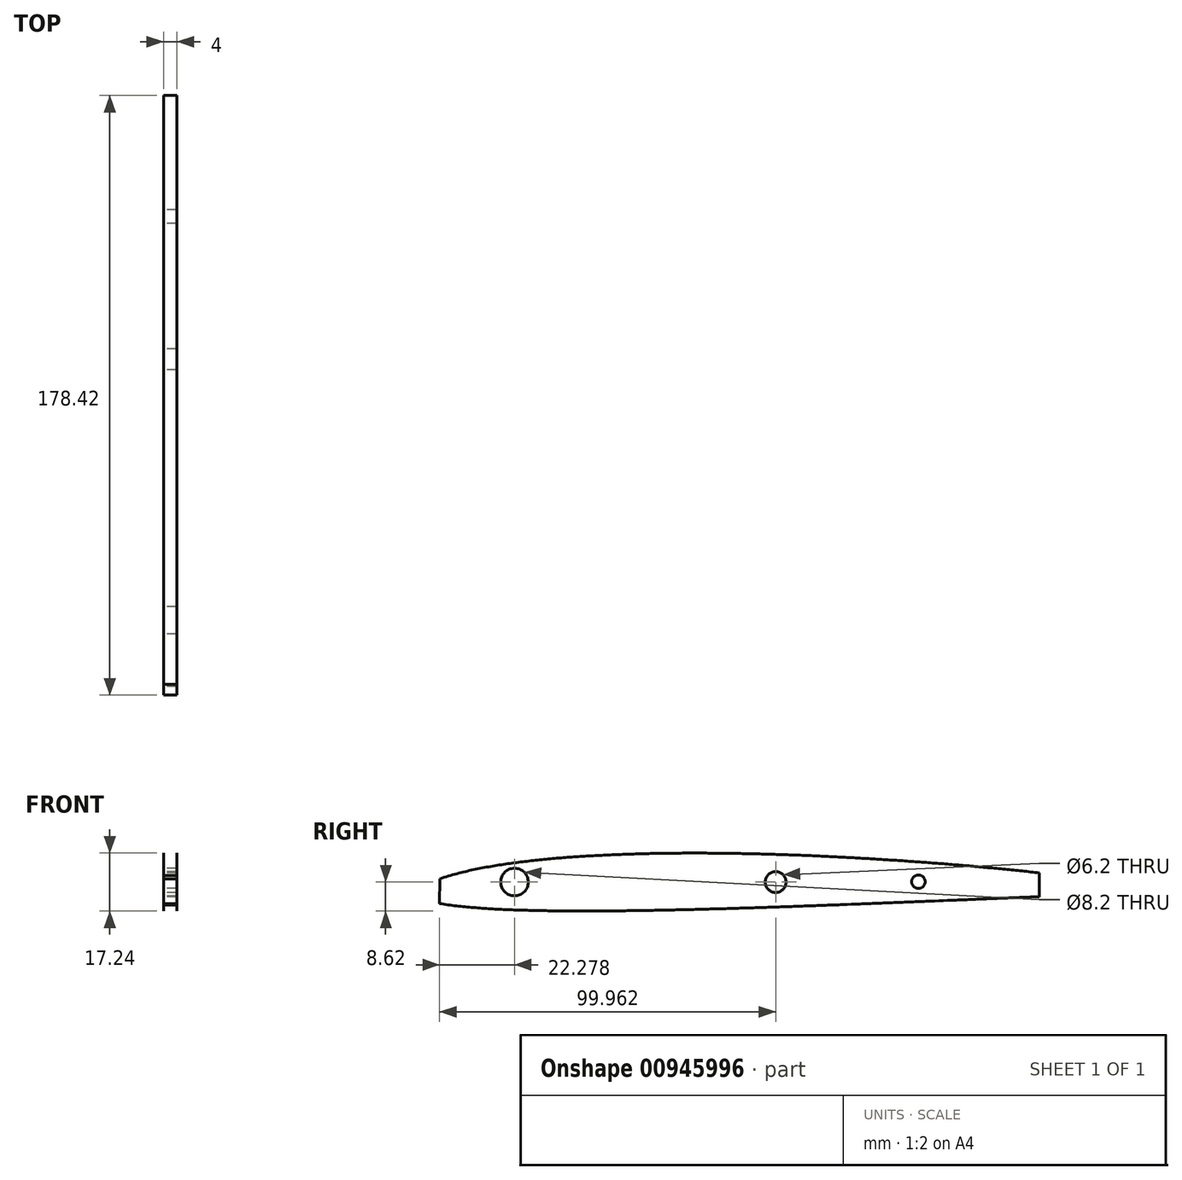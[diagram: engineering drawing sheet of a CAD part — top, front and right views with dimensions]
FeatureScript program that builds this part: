
annotation { "Feature Type Name" : "Feature", "Feature Type Description" : "" }
export const myFeature = defineFeature(function(context is Context, id is Id, definition is map)
    precondition{}
    {
        {
            var Q0;
            Q0=qCreatedBy(makeId("Right.planeOp"),FACE);
            var sketch = newSketch(context, id + "F0", { "sketchPlane" : qUnion([Q0])});
            skLineSegment(sketch, "E0", {"start": v(127, -3.95) * mm, "end": v(126.92, -3.95) * mm});
            skLineSegment(sketch, "E1", {"start": v(126.92, -3.95) * mm, "end": v(126.83, -3.94) * mm});
            skLineSegment(sketch, "E2", {"start": v(126.83, -3.94) * mm, "end": v(126.75, -3.93) * mm});
            skLineSegment(sketch, "E3", {"start": v(126.75, -3.93) * mm, "end": v(126.67, -3.93) * mm});
            skLineSegment(sketch, "E4", {"start": v(126.67, -3.93) * mm, "end": v(126.59, -3.92) * mm});
            skLineSegment(sketch, "E5", {"start": v(126.59, -3.92) * mm, "end": v(126.5, -3.91) * mm});
            skLineSegment(sketch, "E6", {"start": v(126.5, -3.91) * mm, "end": v(126.42, -3.9) * mm});
            skLineSegment(sketch, "E7", {"start": v(126.42, -3.9) * mm, "end": v(126.34, -3.9) * mm});
            skLineSegment(sketch, "E8", {"start": v(126.34, -3.9) * mm, "end": v(126.26, -3.9) * mm});
            skLineSegment(sketch, "E9", {"start": v(126.26, -3.9) * mm, "end": v(125.93, -3.86) * mm});
            skLineSegment(sketch, "E10", {"start": v(125.93, -3.86) * mm, "end": v(125.69, -3.84) * mm});
            skLineSegment(sketch, "E11", {"start": v(125.69, -3.84) * mm, "end": v(125.44, -3.82) * mm});
            skLineSegment(sketch, "E12", {"start": v(125.44, -3.82) * mm, "end": v(125.2, -3.8) * mm});
            skLineSegment(sketch, "E13", {"start": v(125.2, -3.8) * mm, "end": v(124.96, -3.77) * mm});
            skLineSegment(sketch, "E14", {"start": v(124.96, -3.77) * mm, "end": v(124.71, -3.75) * mm});
            skLineSegment(sketch, "E15", {"start": v(124.71, -3.75) * mm, "end": v(124.47, -3.72) * mm});
            skLineSegment(sketch, "E16", {"start": v(124.47, -3.72) * mm, "end": v(124.23, -3.7) * mm});
            skLineSegment(sketch, "E17", {"start": v(124.23, -3.7) * mm, "end": v(123.98, -3.67) * mm});
            skLineSegment(sketch, "E18", {"start": v(123.98, -3.67) * mm, "end": v(123.35, -3.6) * mm});
            skLineSegment(sketch, "E19", {"start": v(123.35, -3.6) * mm, "end": v(122.95, -3.56) * mm});
            skLineSegment(sketch, "E20", {"start": v(122.95, -3.56) * mm, "end": v(122.56, -3.52) * mm});
            skLineSegment(sketch, "E21", {"start": v(122.56, -3.52) * mm, "end": v(122.17, -3.48) * mm});
            skLineSegment(sketch, "E22", {"start": v(122.17, -3.48) * mm, "end": v(121.77, -3.43) * mm});
            skLineSegment(sketch, "E23", {"start": v(121.77, -3.43) * mm, "end": v(121.38, -3.39) * mm});
            skLineSegment(sketch, "E24", {"start": v(121.38, -3.39) * mm, "end": v(120.98, -3.34) * mm});
            skLineSegment(sketch, "E25", {"start": v(120.98, -3.34) * mm, "end": v(120.59, -3.3) * mm});
            skLineSegment(sketch, "E26", {"start": v(120.59, -3.3) * mm, "end": v(120.2, -3.25) * mm});
            skLineSegment(sketch, "E27", {"start": v(120.2, -3.25) * mm, "end": v(119.8, -3.2) * mm});
            skLineSegment(sketch, "E28", {"start": v(119.8, -3.2) * mm, "end": v(119.27, -3.14) * mm});
            skLineSegment(sketch, "E29", {"start": v(119.27, -3.14) * mm, "end": v(118.73, -3.07) * mm});
            skLineSegment(sketch, "E30", {"start": v(118.73, -3.07) * mm, "end": v(118.2, -3) * mm});
            skLineSegment(sketch, "E31", {"start": v(118.2, -3) * mm, "end": v(117.67, -2.94) * mm});
            skLineSegment(sketch, "E32", {"start": v(117.67, -2.94) * mm, "end": v(117.13, -2.87) * mm});
            skLineSegment(sketch, "E33", {"start": v(117.13, -2.87) * mm, "end": v(116.6, -2.8) * mm});
            skLineSegment(sketch, "E34", {"start": v(116.6, -2.8) * mm, "end": v(116.07, -2.74) * mm});
            skLineSegment(sketch, "E35", {"start": v(116.07, -2.74) * mm, "end": v(115.53, -2.67) * mm});
            skLineSegment(sketch, "E36", {"start": v(115.53, -2.67) * mm, "end": v(115, -2.6) * mm});
            skLineSegment(sketch, "E37", {"start": v(115, -2.6) * mm, "end": v(114.47, -2.54) * mm});
            skLineSegment(sketch, "E38", {"start": v(114.47, -2.54) * mm, "end": v(113.8, -2.45) * mm});
            skLineSegment(sketch, "E39", {"start": v(113.8, -2.45) * mm, "end": v(113.14, -2.37) * mm});
            skLineSegment(sketch, "E40", {"start": v(113.14, -2.37) * mm, "end": v(112.48, -2.28) * mm});
            skLineSegment(sketch, "E41", {"start": v(112.48, -2.28) * mm, "end": v(111.82, -2.2) * mm});
            skLineSegment(sketch, "E42", {"start": v(111.82, -2.2) * mm, "end": v(111.16, -2.1) * mm});
            skLineSegment(sketch, "E43", {"start": v(111.16, -2.1) * mm, "end": v(110.5, -2.02) * mm});
            skLineSegment(sketch, "E44", {"start": v(110.5, -2.02) * mm, "end": v(109.84, -1.93) * mm});
            skLineSegment(sketch, "E45", {"start": v(109.84, -1.93) * mm, "end": v(109.17, -1.84) * mm});
            skLineSegment(sketch, "E46", {"start": v(109.17, -1.84) * mm, "end": v(108.51, -1.75) * mm});
            skLineSegment(sketch, "E47", {"start": v(108.51, -1.75) * mm, "end": v(107.07, -1.56) * mm});
            skLineSegment(sketch, "E48", {"start": v(107.07, -1.56) * mm, "end": v(106.3, -1.46) * mm});
            skLineSegment(sketch, "E49", {"start": v(106.3, -1.46) * mm, "end": v(105.52, -1.35) * mm});
            skLineSegment(sketch, "E50", {"start": v(105.52, -1.35) * mm, "end": v(104.74, -1.25) * mm});
            skLineSegment(sketch, "E51", {"start": v(104.74, -1.25) * mm, "end": v(103.96, -1.14) * mm});
            skLineSegment(sketch, "E52", {"start": v(103.96, -1.14) * mm, "end": v(103.19, -1.04) * mm});
            skLineSegment(sketch, "E53", {"start": v(103.19, -1.04) * mm, "end": v(102.4, -0.93) * mm});
            skLineSegment(sketch, "E54", {"start": v(102.4, -0.93) * mm, "end": v(101.63, -0.82) * mm});
            skLineSegment(sketch, "E55", {"start": v(101.63, -0.82) * mm, "end": v(100.85, -0.72) * mm});
            skLineSegment(sketch, "E56", {"start": v(100.85, -0.72) * mm, "end": v(100.08, -0.61) * mm});
            skLineSegment(sketch, "E57", {"start": v(100.08, -0.61) * mm, "end": v(99.2, -0.5) * mm});
            skLineSegment(sketch, "E58", {"start": v(99.2, -0.5) * mm, "end": v(98.32, -0.38) * mm});
            skLineSegment(sketch, "E59", {"start": v(98.32, -0.38) * mm, "end": v(97.43, -0.26) * mm});
            skLineSegment(sketch, "E60", {"start": v(97.43, -0.26) * mm, "end": v(96.55, -0.14) * mm});
            skLineSegment(sketch, "E61", {"start": v(96.55, -0.14) * mm, "end": v(95.67, -0.02) * mm});
            skLineSegment(sketch, "E62", {"start": v(95.67, -0.02) * mm, "end": v(94.8, 0.1) * mm});
            skLineSegment(sketch, "E63", {"start": v(94.8, 0.1) * mm, "end": v(93.91, 0.22) * mm});
            skLineSegment(sketch, "E64", {"start": v(93.91, 0.22) * mm, "end": v(93.03, 0.34) * mm});
            skLineSegment(sketch, "E65", {"start": v(93.03, 0.34) * mm, "end": v(92.15, 0.45) * mm});
            skLineSegment(sketch, "E66", {"start": v(92.15, 0.45) * mm, "end": v(90.3, 0.7) * mm});
            skLineSegment(sketch, "E67", {"start": v(90.3, 0.7) * mm, "end": v(89.33, 0.83) * mm});
            skLineSegment(sketch, "E68", {"start": v(89.33, 0.83) * mm, "end": v(88.36, 0.96) * mm});
            skLineSegment(sketch, "E69", {"start": v(88.36, 0.96) * mm, "end": v(87.39, 1.09) * mm});
            skLineSegment(sketch, "E70", {"start": v(87.39, 1.09) * mm, "end": v(86.42, 1.22) * mm});
            skLineSegment(sketch, "E71", {"start": v(86.42, 1.22) * mm, "end": v(85.44, 1.34) * mm});
            skLineSegment(sketch, "E72", {"start": v(85.44, 1.34) * mm, "end": v(84.47, 1.47) * mm});
            skLineSegment(sketch, "E73", {"start": v(84.47, 1.47) * mm, "end": v(83.5, 1.6) * mm});
            skLineSegment(sketch, "E74", {"start": v(83.5, 1.6) * mm, "end": v(82.53, 1.72) * mm});
            skLineSegment(sketch, "E75", {"start": v(82.53, 1.72) * mm, "end": v(81.56, 1.85) * mm});
            skLineSegment(sketch, "E76", {"start": v(81.56, 1.85) * mm, "end": v(80.51, 1.98) * mm});
            skLineSegment(sketch, "E77", {"start": v(80.51, 1.98) * mm, "end": v(79.46, 2.12) * mm});
            skLineSegment(sketch, "E78", {"start": v(79.46, 2.12) * mm, "end": v(78.41, 2.25) * mm});
            skLineSegment(sketch, "E79", {"start": v(78.41, 2.25) * mm, "end": v(77.36, 2.38) * mm});
            skLineSegment(sketch, "E80", {"start": v(77.36, 2.38) * mm, "end": v(76.31, 2.51) * mm});
            skLineSegment(sketch, "E81", {"start": v(76.31, 2.51) * mm, "end": v(75.26, 2.64) * mm});
            skLineSegment(sketch, "E82", {"start": v(75.26, 2.64) * mm, "end": v(74.21, 2.77) * mm});
            skLineSegment(sketch, "E83", {"start": v(74.21, 2.77) * mm, "end": v(73.17, 2.9) * mm});
            skLineSegment(sketch, "E84", {"start": v(73.17, 2.9) * mm, "end": v(72.12, 3.03) * mm});
            skLineSegment(sketch, "E85", {"start": v(72.12, 3.03) * mm, "end": v(69.95, 3.29) * mm});
            skLineSegment(sketch, "E86", {"start": v(69.95, 3.29) * mm, "end": v(68.83, 3.42) * mm});
            skLineSegment(sketch, "E87", {"start": v(68.83, 3.42) * mm, "end": v(67.72, 3.55) * mm});
            skLineSegment(sketch, "E88", {"start": v(67.72, 3.55) * mm, "end": v(66.6, 3.68) * mm});
            skLineSegment(sketch, "E89", {"start": v(66.6, 3.68) * mm, "end": v(65.48, 3.8) * mm});
            skLineSegment(sketch, "E90", {"start": v(65.48, 3.8) * mm, "end": v(64.37, 3.93) * mm});
            skLineSegment(sketch, "E91", {"start": v(64.37, 3.93) * mm, "end": v(63.25, 4.06) * mm});
            skLineSegment(sketch, "E92", {"start": v(63.25, 4.06) * mm, "end": v(62.14, 4.18) * mm});
            skLineSegment(sketch, "E93", {"start": v(62.14, 4.18) * mm, "end": v(61.02, 4.3) * mm});
            skLineSegment(sketch, "E94", {"start": v(61.02, 4.3) * mm, "end": v(58.73, 4.55) * mm});
            skLineSegment(sketch, "E95", {"start": v(58.73, 4.55) * mm, "end": v(57.56, 4.68) * mm});
            skLineSegment(sketch, "E96", {"start": v(57.56, 4.68) * mm, "end": v(56.38, 4.8) * mm});
            skLineSegment(sketch, "E97", {"start": v(56.38, 4.8) * mm, "end": v(55.21, 4.92) * mm});
            skLineSegment(sketch, "E98", {"start": v(55.21, 4.92) * mm, "end": v(54.04, 5.04) * mm});
            skLineSegment(sketch, "E99", {"start": v(54.04, 5.04) * mm, "end": v(52.86, 5.16) * mm});
            skLineSegment(sketch, "E100", {"start": v(52.86, 5.16) * mm, "end": v(51.7, 5.27) * mm});
            skLineSegment(sketch, "E101", {"start": v(51.7, 5.27) * mm, "end": v(50.52, 5.39) * mm});
            skLineSegment(sketch, "E102", {"start": v(50.52, 5.39) * mm, "end": v(49.34, 5.5) * mm});
            skLineSegment(sketch, "E103", {"start": v(49.34, 5.5) * mm, "end": v(48.17, 5.61) * mm});
            skLineSegment(sketch, "E104", {"start": v(48.17, 5.61) * mm, "end": v(46.95, 5.73) * mm});
            skLineSegment(sketch, "E105", {"start": v(46.95, 5.73) * mm, "end": v(45.73, 5.84) * mm});
            skLineSegment(sketch, "E106", {"start": v(45.73, 5.84) * mm, "end": v(44.51, 5.95) * mm});
            skLineSegment(sketch, "E107", {"start": v(44.51, 5.95) * mm, "end": v(43.3, 6.06) * mm});
            skLineSegment(sketch, "E108", {"start": v(43.3, 6.06) * mm, "end": v(42.07, 6.17) * mm});
            skLineSegment(sketch, "E109", {"start": v(42.07, 6.17) * mm, "end": v(40.85, 6.28) * mm});
            skLineSegment(sketch, "E110", {"start": v(40.85, 6.28) * mm, "end": v(39.63, 6.39) * mm});
            skLineSegment(sketch, "E111", {"start": v(39.63, 6.39) * mm, "end": v(38.41, 6.5) * mm});
            skLineSegment(sketch, "E112", {"start": v(38.41, 6.5) * mm, "end": v(37.2, 6.6) * mm});
            skLineSegment(sketch, "E113", {"start": v(37.2, 6.6) * mm, "end": v(35.97, 6.7) * mm});
            skLineSegment(sketch, "E114", {"start": v(35.97, 6.7) * mm, "end": v(34.72, 6.8) * mm});
            skLineSegment(sketch, "E115", {"start": v(34.72, 6.8) * mm, "end": v(33.46, 6.9) * mm});
            skLineSegment(sketch, "E116", {"start": v(33.46, 6.9) * mm, "end": v(32.2, 7) * mm});
            skLineSegment(sketch, "E117", {"start": v(32.2, 7) * mm, "end": v(30.95, 7.1) * mm});
            skLineSegment(sketch, "E118", {"start": v(30.95, 7.1) * mm, "end": v(29.7, 7.2) * mm});
            skLineSegment(sketch, "E119", {"start": v(29.7, 7.2) * mm, "end": v(28.44, 7.29) * mm});
            skLineSegment(sketch, "E120", {"start": v(28.44, 7.29) * mm, "end": v(27.19, 7.38) * mm});
            skLineSegment(sketch, "E121", {"start": v(27.19, 7.38) * mm, "end": v(25.93, 7.47) * mm});
            skLineSegment(sketch, "E122", {"start": v(25.93, 7.47) * mm, "end": v(24.68, 7.56) * mm});
            skLineSegment(sketch, "E123", {"start": v(24.68, 7.56) * mm, "end": v(23.42, 7.65) * mm});
            skLineSegment(sketch, "E124", {"start": v(23.42, 7.65) * mm, "end": v(22.15, 7.74) * mm});
            skLineSegment(sketch, "E125", {"start": v(22.15, 7.74) * mm, "end": v(20.87, 7.83) * mm});
            skLineSegment(sketch, "E126", {"start": v(20.87, 7.83) * mm, "end": v(19.6, 7.91) * mm});
            skLineSegment(sketch, "E127", {"start": v(19.6, 7.91) * mm, "end": v(18.31, 8) * mm});
            skLineSegment(sketch, "E128", {"start": v(18.31, 8) * mm, "end": v(17.04, 8.08) * mm});
            skLineSegment(sketch, "E129", {"start": v(17.04, 8.08) * mm, "end": v(15.76, 8.16) * mm});
            skLineSegment(sketch, "E130", {"start": v(15.76, 8.16) * mm, "end": v(14.48, 8.24) * mm});
            skLineSegment(sketch, "E131", {"start": v(14.48, 8.24) * mm, "end": v(13.2, 8.32) * mm});
            skLineSegment(sketch, "E132", {"start": v(13.2, 8.32) * mm, "end": v(11.93, 8.4) * mm});
            skLineSegment(sketch, "E133", {"start": v(11.93, 8.4) * mm, "end": v(9.37, 8.55) * mm});
            skLineSegment(sketch, "E134", {"start": v(9.37, 8.55) * mm, "end": v(8.08, 8.63) * mm});
            skLineSegment(sketch, "E135", {"start": v(8.08, 8.63) * mm, "end": v(6.8, 8.7) * mm});
            skLineSegment(sketch, "E136", {"start": v(6.8, 8.7) * mm, "end": v(5.51, 8.77) * mm});
            skLineSegment(sketch, "E137", {"start": v(5.51, 8.77) * mm, "end": v(4.23, 8.84) * mm});
            skLineSegment(sketch, "E138", {"start": v(4.23, 8.84) * mm, "end": v(2.94, 8.9) * mm});
            skLineSegment(sketch, "E139", {"start": v(2.94, 8.9) * mm, "end": v(1.66, 8.97) * mm});
            skLineSegment(sketch, "E140", {"start": v(1.66, 8.97) * mm, "end": v(0.38, 9.04) * mm});
            skLineSegment(sketch, "E141", {"start": v(0.38, 9.04) * mm, "end": v(-0.9, 9.1) * mm});
            skLineSegment(sketch, "E142", {"start": v(-0.9, 9.1) * mm, "end": v(-3.47, 9.22) * mm});
            skLineSegment(sketch, "E143", {"start": v(-3.47, 9.22) * mm, "end": v(-4.75, 9.28) * mm});
            skLineSegment(sketch, "E144", {"start": v(-4.75, 9.28) * mm, "end": v(-6.02, 9.33) * mm});
            skLineSegment(sketch, "E145", {"start": v(-6.02, 9.33) * mm, "end": v(-7.3, 9.39) * mm});
            skLineSegment(sketch, "E146", {"start": v(-7.3, 9.39) * mm, "end": v(-8.58, 9.44) * mm});
            skLineSegment(sketch, "E147", {"start": v(-8.58, 9.44) * mm, "end": v(-9.86, 9.5) * mm});
            skLineSegment(sketch, "E148", {"start": v(-9.86, 9.5) * mm, "end": v(-11.14, 9.54) * mm});
            skLineSegment(sketch, "E149", {"start": v(-11.14, 9.54) * mm, "end": v(-12.41, 9.59) * mm});
            skLineSegment(sketch, "E150", {"start": v(-12.41, 9.59) * mm, "end": v(-13.7, 9.63) * mm});
            skLineSegment(sketch, "E151", {"start": v(-13.7, 9.63) * mm, "end": v(-16.23, 9.71) * mm});
            skLineSegment(sketch, "E152", {"start": v(-16.23, 9.71) * mm, "end": v(-17.49, 9.75) * mm});
            skLineSegment(sketch, "E153", {"start": v(-17.49, 9.75) * mm, "end": v(-18.74, 9.79) * mm});
            skLineSegment(sketch, "E154", {"start": v(-18.74, 9.79) * mm, "end": v(-20, 9.82) * mm});
            skLineSegment(sketch, "E155", {"start": v(-20, 9.82) * mm, "end": v(-21.26, 9.86) * mm});
            skLineSegment(sketch, "E156", {"start": v(-21.26, 9.86) * mm, "end": v(-22.52, 9.89) * mm});
            skLineSegment(sketch, "E157", {"start": v(-22.52, 9.89) * mm, "end": v(-23.78, 9.92) * mm});
            skLineSegment(sketch, "E158", {"start": v(-23.78, 9.92) * mm, "end": v(-25.04, 9.94) * mm});
            skLineSegment(sketch, "E159", {"start": v(-25.04, 9.94) * mm, "end": v(-26.3, 9.97) * mm});
            skLineSegment(sketch, "E160", {"start": v(-26.3, 9.97) * mm, "end": v(-28.78, 10.01) * mm});
            skLineSegment(sketch, "E161", {"start": v(-28.78, 10.01) * mm, "end": v(-30.01, 10.03) * mm});
            skLineSegment(sketch, "E162", {"start": v(-30.01, 10.03) * mm, "end": v(-31.24, 10.05) * mm});
            skLineSegment(sketch, "E163", {"start": v(-31.24, 10.05) * mm, "end": v(-32.47, 10.07) * mm});
            skLineSegment(sketch, "E164", {"start": v(-32.47, 10.07) * mm, "end": v(-33.7, 10.08) * mm});
            skLineSegment(sketch, "E165", {"start": v(-33.7, 10.08) * mm, "end": v(-34.92, 10.1) * mm});
            skLineSegment(sketch, "E166", {"start": v(-34.92, 10.1) * mm, "end": v(-36.15, 10.1) * mm});
            skLineSegment(sketch, "E167", {"start": v(-36.15, 10.1) * mm, "end": v(-37.38, 10.1) * mm});
            skLineSegment(sketch, "E168", {"start": v(-37.38, 10.1) * mm, "end": v(-38.6, 10.11) * mm});
            skLineSegment(sketch, "E169", {"start": v(-38.6, 10.11) * mm, "end": v(-39.83, 10.12) * mm});
            skLineSegment(sketch, "E170", {"start": v(-39.83, 10.12) * mm, "end": v(-41.01, 10.12) * mm});
            skLineSegment(sketch, "E171", {"start": v(-41.01, 10.12) * mm, "end": v(-42.2, 10.12) * mm});
            skLineSegment(sketch, "E172", {"start": v(-42.2, 10.12) * mm, "end": v(-43.38, 10.11) * mm});
            skLineSegment(sketch, "E173", {"start": v(-43.38, 10.11) * mm, "end": v(-44.56, 10.1) * mm});
            skLineSegment(sketch, "E174", {"start": v(-44.56, 10.1) * mm, "end": v(-45.74, 10.1) * mm});
            skLineSegment(sketch, "E175", {"start": v(-45.74, 10.1) * mm, "end": v(-46.93, 10.09) * mm});
            skLineSegment(sketch, "E176", {"start": v(-46.93, 10.09) * mm, "end": v(-48.1, 10.08) * mm});
            skLineSegment(sketch, "E177", {"start": v(-48.1, 10.08) * mm, "end": v(-49.3, 10.06) * mm});
            skLineSegment(sketch, "E178", {"start": v(-49.3, 10.06) * mm, "end": v(-50.47, 10.05) * mm});
            skLineSegment(sketch, "E179", {"start": v(-50.47, 10.05) * mm, "end": v(-51.66, 10.03) * mm});
            skLineSegment(sketch, "E180", {"start": v(-51.66, 10.03) * mm, "end": v(-52.78, 10) * mm});
            skLineSegment(sketch, "E181", {"start": v(-52.78, 10) * mm, "end": v(-53.91, 9.98) * mm});
            skLineSegment(sketch, "E182", {"start": v(-53.91, 9.98) * mm, "end": v(-55.04, 9.96) * mm});
            skLineSegment(sketch, "E183", {"start": v(-55.04, 9.96) * mm, "end": v(-56.17, 9.93) * mm});
            skLineSegment(sketch, "E184", {"start": v(-56.17, 9.93) * mm, "end": v(-57.3, 9.9) * mm});
            skLineSegment(sketch, "E185", {"start": v(-57.3, 9.9) * mm, "end": v(-58.42, 9.87) * mm});
            skLineSegment(sketch, "E186", {"start": v(-58.42, 9.87) * mm, "end": v(-59.55, 9.83) * mm});
            skLineSegment(sketch, "E187", {"start": v(-59.55, 9.83) * mm, "end": v(-60.68, 9.8) * mm});
            skLineSegment(sketch, "E188", {"start": v(-60.68, 9.8) * mm, "end": v(-61.8, 9.76) * mm});
            skLineSegment(sketch, "E189", {"start": v(-61.8, 9.76) * mm, "end": v(-62.93, 9.72) * mm});
            skLineSegment(sketch, "E190", {"start": v(-62.93, 9.72) * mm, "end": v(-64, 9.68) * mm});
            skLineSegment(sketch, "E191", {"start": v(-64, 9.68) * mm, "end": v(-65.05, 9.63) * mm});
            skLineSegment(sketch, "E192", {"start": v(-65.05, 9.63) * mm, "end": v(-66.11, 9.59) * mm});
            skLineSegment(sketch, "E193", {"start": v(-66.11, 9.59) * mm, "end": v(-67.18, 9.54) * mm});
            skLineSegment(sketch, "E194", {"start": v(-67.18, 9.54) * mm, "end": v(-68.24, 9.49) * mm});
            skLineSegment(sketch, "E195", {"start": v(-68.24, 9.49) * mm, "end": v(-69.3, 9.43) * mm});
            skLineSegment(sketch, "E196", {"start": v(-69.3, 9.43) * mm, "end": v(-70.36, 9.38) * mm});
            skLineSegment(sketch, "E197", {"start": v(-70.36, 9.38) * mm, "end": v(-71.42, 9.32) * mm});
            skLineSegment(sketch, "E198", {"start": v(-71.42, 9.32) * mm, "end": v(-72.48, 9.26) * mm});
            skLineSegment(sketch, "E199", {"start": v(-72.48, 9.26) * mm, "end": v(-74.53, 9.13) * mm});
            skLineSegment(sketch, "E200", {"start": v(-74.53, 9.13) * mm, "end": v(-75.51, 9.07) * mm});
            skLineSegment(sketch, "E201", {"start": v(-75.51, 9.07) * mm, "end": v(-76.5, 9) * mm});
            skLineSegment(sketch, "E202", {"start": v(-76.5, 9) * mm, "end": v(-77.48, 8.93) * mm});
            skLineSegment(sketch, "E203", {"start": v(-77.48, 8.93) * mm, "end": v(-78.46, 8.86) * mm});
            skLineSegment(sketch, "E204", {"start": v(-78.46, 8.86) * mm, "end": v(-79.45, 8.79) * mm});
            skLineSegment(sketch, "E205", {"start": v(-79.45, 8.79) * mm, "end": v(-80.43, 8.71) * mm});
            skLineSegment(sketch, "E206", {"start": v(-80.43, 8.71) * mm, "end": v(-81.42, 8.63) * mm});
            skLineSegment(sketch, "E207", {"start": v(-81.42, 8.63) * mm, "end": v(-82.4, 8.55) * mm});
            skLineSegment(sketch, "E208", {"start": v(-82.4, 8.55) * mm, "end": v(-84.28, 8.38) * mm});
            skLineSegment(sketch, "E209", {"start": v(-84.28, 8.38) * mm, "end": v(-85.18, 8.3) * mm});
            skLineSegment(sketch, "E210", {"start": v(-85.18, 8.3) * mm, "end": v(-86.08, 8.2) * mm});
            skLineSegment(sketch, "E211", {"start": v(-86.08, 8.2) * mm, "end": v(-86.98, 8.11) * mm});
            skLineSegment(sketch, "E212", {"start": v(-86.98, 8.11) * mm, "end": v(-87.88, 8.02) * mm});
            skLineSegment(sketch, "E213", {"start": v(-87.88, 8.02) * mm, "end": v(-88.77, 7.92) * mm});
            skLineSegment(sketch, "E214", {"start": v(-88.77, 7.92) * mm, "end": v(-89.67, 7.82) * mm});
            skLineSegment(sketch, "E215", {"start": v(-89.67, 7.82) * mm, "end": v(-90.57, 7.72) * mm});
            skLineSegment(sketch, "E216", {"start": v(-90.57, 7.72) * mm, "end": v(-91.47, 7.61) * mm});
            skLineSegment(sketch, "E217", {"start": v(-91.47, 7.61) * mm, "end": v(-92.37, 7.5) * mm});
            skLineSegment(sketch, "E218", {"start": v(-92.37, 7.5) * mm, "end": v(-93.17, 7.4) * mm});
            skLineSegment(sketch, "E219", {"start": v(-93.17, 7.4) * mm, "end": v(-93.98, 7.3) * mm});
            skLineSegment(sketch, "E220", {"start": v(-93.98, 7.3) * mm, "end": v(-94.78, 7.2) * mm});
            skLineSegment(sketch, "E221", {"start": v(-94.78, 7.2) * mm, "end": v(-95.59, 7.08) * mm});
            skLineSegment(sketch, "E222", {"start": v(-95.59, 7.08) * mm, "end": v(-96.4, 6.97) * mm});
            skLineSegment(sketch, "E223", {"start": v(-96.4, 6.97) * mm, "end": v(-97.2, 6.85) * mm});
            skLineSegment(sketch, "E224", {"start": v(-97.2, 6.85) * mm, "end": v(-98, 6.73) * mm});
            skLineSegment(sketch, "E225", {"start": v(-98, 6.73) * mm, "end": v(-98.81, 6.6) * mm});
            skLineSegment(sketch, "E226", {"start": v(-98.81, 6.6) * mm, "end": v(-99.62, 6.48) * mm});
            skLineSegment(sketch, "E227", {"start": v(-99.62, 6.48) * mm, "end": v(-100.42, 6.35) * mm});
            skLineSegment(sketch, "E228", {"start": v(-100.42, 6.35) * mm, "end": v(-101.13, 6.23) * mm});
            skLineSegment(sketch, "E229", {"start": v(-101.13, 6.23) * mm, "end": v(-101.83, 6.1) * mm});
            skLineSegment(sketch, "E230", {"start": v(-101.83, 6.1) * mm, "end": v(-102.54, 5.98) * mm});
            skLineSegment(sketch, "E231", {"start": v(-102.54, 5.98) * mm, "end": v(-103.25, 5.85) * mm});
            skLineSegment(sketch, "E232", {"start": v(-103.25, 5.85) * mm, "end": v(-103.95, 5.72) * mm});
            skLineSegment(sketch, "E233", {"start": v(-103.95, 5.72) * mm, "end": v(-104.66, 5.59) * mm});
            skLineSegment(sketch, "E234", {"start": v(-104.66, 5.59) * mm, "end": v(-105.37, 5.45) * mm});
            skLineSegment(sketch, "E235", {"start": v(-105.37, 5.45) * mm, "end": v(-106.07, 5.3) * mm});
            skLineSegment(sketch, "E236", {"start": v(-106.07, 5.3) * mm, "end": v(-106.78, 5.16) * mm});
            skLineSegment(sketch, "E237", {"start": v(-108.09, 4.87) * mm, "end": v(-108.69, 4.73) * mm});
            skLineSegment(sketch, "E238", {"start": v(-108.69, 4.73) * mm, "end": v(-109.3, 4.6) * mm});
            skLineSegment(sketch, "E239", {"start": v(-109.3, 4.6) * mm, "end": v(-109.9, 4.45) * mm});
            skLineSegment(sketch, "E240", {"start": v(-109.9, 4.45) * mm, "end": v(-110.5, 4.3) * mm});
            skLineSegment(sketch, "E241", {"start": v(-110.5, 4.3) * mm, "end": v(-111.1, 4.15) * mm});
            skLineSegment(sketch, "E242", {"start": v(-111.1, 4.15) * mm, "end": v(-111.7, 4) * mm});
            skLineSegment(sketch, "E243", {"start": v(-111.7, 4) * mm, "end": v(-112.3, 3.84) * mm});
            skLineSegment(sketch, "E244", {"start": v(-112.3, 3.84) * mm, "end": v(-112.9, 3.67) * mm});
            skLineSegment(sketch, "E245", {"start": v(-112.9, 3.67) * mm, "end": v(-113.5, 3.5) * mm});
            skLineSegment(sketch, "E246", {"start": v(-113.5, 3.5) * mm, "end": v(-114, 3.36) * mm});
            skLineSegment(sketch, "E247", {"start": v(-114, 3.36) * mm, "end": v(-114.5, 3.21) * mm});
            skLineSegment(sketch, "E248", {"start": v(-114.5, 3.21) * mm, "end": v(-115, 3.06) * mm});
            skLineSegment(sketch, "E249", {"start": v(-115, 3.06) * mm, "end": v(-115.49, 2.9) * mm});
            skLineSegment(sketch, "E250", {"start": v(-115.49, 2.9) * mm, "end": v(-115.98, 2.74) * mm});
            skLineSegment(sketch, "E251", {"start": v(-115.98, 2.74) * mm, "end": v(-116.48, 2.58) * mm});
            skLineSegment(sketch, "E252", {"start": v(-116.48, 2.58) * mm, "end": v(-116.97, 2.41) * mm});
            skLineSegment(sketch, "E253", {"start": v(-116.97, 2.41) * mm, "end": v(-117.47, 2.24) * mm});
            skLineSegment(sketch, "E254", {"start": v(-117.47, 2.24) * mm, "end": v(-117.96, 2.06) * mm});
            skLineSegment(sketch, "E255", {"start": v(-117.96, 2.06) * mm, "end": v(-118.46, 1.88) * mm});
            skLineSegment(sketch, "E256", {"start": v(-118.46, 1.88) * mm, "end": v(-118.9, 1.71) * mm});
            skLineSegment(sketch, "E257", {"start": v(-118.9, 1.71) * mm, "end": v(-119.32, 1.54) * mm});
            skLineSegment(sketch, "E258", {"start": v(-119.32, 1.54) * mm, "end": v(-119.74, 1.37) * mm});
            skLineSegment(sketch, "E259", {"start": v(-119.74, 1.37) * mm, "end": v(-120.14, 1.2) * mm});
            skLineSegment(sketch, "E260", {"start": v(-120.14, 1.2) * mm, "end": v(-120.53, 1.03) * mm});
            skLineSegment(sketch, "E261", {"start": v(-120.53, 1.03) * mm, "end": v(-120.9, 0.86) * mm});
            skLineSegment(sketch, "E262", {"start": v(-120.9, 0.86) * mm, "end": v(-121.27, 0.7) * mm});
            skLineSegment(sketch, "E263", {"start": v(-121.27, 0.7) * mm, "end": v(-121.63, 0.53) * mm});
            skLineSegment(sketch, "E264", {"start": v(-121.63, 0.53) * mm, "end": v(-121.97, 0.36) * mm});
            skLineSegment(sketch, "E265", {"start": v(-121.97, 0.36) * mm, "end": v(-122.3, 0.19) * mm});
            skLineSegment(sketch, "E266", {"start": v(-122.3, 0.19) * mm, "end": v(-122.62, 0.02) * mm});
            skLineSegment(sketch, "E267", {"start": v(-122.62, 0.02) * mm, "end": v(-122.93, -0.15) * mm});
            skLineSegment(sketch, "E268", {"start": v(-122.93, -0.15) * mm, "end": v(-123.23, -0.32) * mm});
            skLineSegment(sketch, "E269", {"start": v(-123.23, -0.32) * mm, "end": v(-123.52, -0.49) * mm});
            skLineSegment(sketch, "E270", {"start": v(-123.52, -0.49) * mm, "end": v(-123.8, -0.66) * mm});
            skLineSegment(sketch, "E271", {"start": v(-123.8, -0.66) * mm, "end": v(-124.06, -0.83) * mm});
            skLineSegment(sketch, "E272", {"start": v(-124.06, -0.83) * mm, "end": v(-124.32, -1) * mm});
            skLineSegment(sketch, "E273", {"start": v(-124.32, -1) * mm, "end": v(-124.57, -1.16) * mm});
            skLineSegment(sketch, "E274", {"start": v(-124.57, -1.16) * mm, "end": v(-124.81, -1.33) * mm});
            skLineSegment(sketch, "E275", {"start": v(-124.81, -1.33) * mm, "end": v(-125.04, -1.5) * mm});
            skLineSegment(sketch, "E276", {"start": v(-125.04, -1.5) * mm, "end": v(-125.24, -1.66) * mm});
            skLineSegment(sketch, "E277", {"start": v(-125.24, -1.66) * mm, "end": v(-125.43, -1.81) * mm});
            skLineSegment(sketch, "E278", {"start": v(-125.43, -1.81) * mm, "end": v(-125.6, -1.97) * mm});
            skLineSegment(sketch, "E279", {"start": v(-125.6, -1.97) * mm, "end": v(-125.78, -2.13) * mm});
            skLineSegment(sketch, "E280", {"start": v(-125.78, -2.13) * mm, "end": v(-125.95, -2.28) * mm});
            skLineSegment(sketch, "E281", {"start": v(-125.95, -2.28) * mm, "end": v(-126.1, -2.44) * mm});
            skLineSegment(sketch, "E282", {"start": v(-126.1, -2.44) * mm, "end": v(-126.26, -2.6) * mm});
            skLineSegment(sketch, "E283", {"start": v(-126.26, -2.6) * mm, "end": v(-126.4, -2.75) * mm});
            skLineSegment(sketch, "E284", {"start": v(-126.4, -2.75) * mm, "end": v(-126.52, -2.91) * mm});
            skLineSegment(sketch, "E285", {"start": v(-126.52, -2.91) * mm, "end": v(-126.64, -3.07) * mm});
            skLineSegment(sketch, "E286", {"start": v(-126.64, -3.07) * mm, "end": v(-126.7, -3.16) * mm});
            skLineSegment(sketch, "E287", {"start": v(-126.7, -3.16) * mm, "end": v(-126.76, -3.24) * mm});
            skLineSegment(sketch, "E288", {"start": v(-126.76, -3.24) * mm, "end": v(-126.81, -3.33) * mm});
            skLineSegment(sketch, "E289", {"start": v(-126.81, -3.33) * mm, "end": v(-126.86, -3.42) * mm});
            skLineSegment(sketch, "E290", {"start": v(-126.86, -3.42) * mm, "end": v(-126.9, -3.51) * mm});
            skLineSegment(sketch, "E291", {"start": v(-126.9, -3.51) * mm, "end": v(-126.93, -3.6) * mm});
            skLineSegment(sketch, "E292", {"start": v(-126.93, -3.6) * mm, "end": v(-126.96, -3.69) * mm});
            skLineSegment(sketch, "E293", {"start": v(-126.96, -3.69) * mm, "end": v(-126.98, -3.78) * mm});
            skLineSegment(sketch, "E294", {"start": v(-126.98, -3.78) * mm, "end": v(-127, -3.87) * mm});
            skLineSegment(sketch, "E295", {"start": v(-127, -3.87) * mm, "end": v(-127, -3.95) * mm});
            skLineSegment(sketch, "E296", {"start": v(-127, -3.95) * mm, "end": v(-127, -3.99) * mm});
            skLineSegment(sketch, "E297", {"start": v(-127, -3.99) * mm, "end": v(-127, -4.02) * mm});
            skLineSegment(sketch, "E298", {"start": v(-127, -4.02) * mm, "end": v(-127, -4.06) * mm});
            skLineSegment(sketch, "E299", {"start": v(-127, -4.06) * mm, "end": v(-127, -4.1) * mm});
            skLineSegment(sketch, "E300", {"start": v(-127, -4.1) * mm, "end": v(-126.99, -4.13) * mm});
            skLineSegment(sketch, "E301", {"start": v(-126.99, -4.13) * mm, "end": v(-126.98, -4.16) * mm});
            skLineSegment(sketch, "E302", {"start": v(-126.98, -4.16) * mm, "end": v(-126.97, -4.2) * mm});
            skLineSegment(sketch, "E303", {"start": v(-126.97, -4.2) * mm, "end": v(-126.96, -4.23) * mm});
            skLineSegment(sketch, "E304", {"start": v(-126.96, -4.23) * mm, "end": v(-126.95, -4.27) * mm});
            skLineSegment(sketch, "E305", {"start": v(-126.95, -4.27) * mm, "end": v(-126.94, -4.3) * mm});
            skLineSegment(sketch, "E306", {"start": v(-126.94, -4.3) * mm, "end": v(-126.89, -4.4) * mm});
            skLineSegment(sketch, "E307", {"start": v(-126.89, -4.4) * mm, "end": v(-126.82, -4.51) * mm});
            skLineSegment(sketch, "E308", {"start": v(-126.82, -4.51) * mm, "end": v(-126.74, -4.62) * mm});
            skLineSegment(sketch, "E309", {"start": v(-126.74, -4.62) * mm, "end": v(-126.65, -4.72) * mm});
            skLineSegment(sketch, "E310", {"start": v(-126.65, -4.72) * mm, "end": v(-126.54, -4.83) * mm});
            skLineSegment(sketch, "E311", {"start": v(-126.54, -4.83) * mm, "end": v(-126.41, -4.93) * mm});
            skLineSegment(sketch, "E312", {"start": v(-126.41, -4.93) * mm, "end": v(-126.27, -5.04) * mm});
            skLineSegment(sketch, "E313", {"start": v(-126.27, -5.04) * mm, "end": v(-126.12, -5.14) * mm});
            skLineSegment(sketch, "E314", {"start": v(-126.12, -5.14) * mm, "end": v(-125.95, -5.25) * mm});
            skLineSegment(sketch, "E315", {"start": v(-125.95, -5.25) * mm, "end": v(-125.77, -5.35) * mm});
            skLineSegment(sketch, "E316", {"start": v(-125.77, -5.35) * mm, "end": v(-125.58, -5.46) * mm});
            skLineSegment(sketch, "E317", {"start": v(-125.58, -5.46) * mm, "end": v(-125.37, -5.57) * mm});
            skLineSegment(sketch, "E318", {"start": v(-125.37, -5.57) * mm, "end": v(-125.15, -5.67) * mm});
            skLineSegment(sketch, "E319", {"start": v(-125.15, -5.67) * mm, "end": v(-124.92, -5.78) * mm});
            skLineSegment(sketch, "E320", {"start": v(-124.92, -5.78) * mm, "end": v(-124.67, -5.89) * mm});
            skLineSegment(sketch, "E321", {"start": v(-124.67, -5.89) * mm, "end": v(-124.4, -6) * mm});
            skLineSegment(sketch, "E322", {"start": v(-124.4, -6) * mm, "end": v(-124.13, -6.1) * mm});
            skLineSegment(sketch, "E323", {"start": v(-124.13, -6.1) * mm, "end": v(-123.84, -6.2) * mm});
            skLineSegment(sketch, "E324", {"start": v(-123.84, -6.2) * mm, "end": v(-123.53, -6.32) * mm});
            skLineSegment(sketch, "E325", {"start": v(-123.53, -6.32) * mm, "end": v(-123.21, -6.42) * mm});
            skLineSegment(sketch, "E326", {"start": v(-123.21, -6.42) * mm, "end": v(-122.9, -6.52) * mm});
            skLineSegment(sketch, "E327", {"start": v(-122.9, -6.52) * mm, "end": v(-122.57, -6.62) * mm});
            skLineSegment(sketch, "E328", {"start": v(-122.57, -6.62) * mm, "end": v(-122.22, -6.72) * mm});
            skLineSegment(sketch, "E329", {"start": v(-122.22, -6.72) * mm, "end": v(-121.86, -6.82) * mm});
            skLineSegment(sketch, "E330", {"start": v(-121.86, -6.82) * mm, "end": v(-121.49, -6.92) * mm});
            skLineSegment(sketch, "E331", {"start": v(-121.49, -6.92) * mm, "end": v(-121.1, -7.02) * mm});
            skLineSegment(sketch, "E332", {"start": v(-121.1, -7.02) * mm, "end": v(-120.7, -7.12) * mm});
            skLineSegment(sketch, "E333", {"start": v(-120.7, -7.12) * mm, "end": v(-120.27, -7.22) * mm});
            skLineSegment(sketch, "E334", {"start": v(-120.27, -7.22) * mm, "end": v(-119.82, -7.31) * mm});
            skLineSegment(sketch, "E335", {"start": v(-119.82, -7.31) * mm, "end": v(-119.36, -7.41) * mm});
            skLineSegment(sketch, "E336", {"start": v(-119.36, -7.41) * mm, "end": v(-118.85, -7.51) * mm});
            skLineSegment(sketch, "E337", {"start": v(-118.85, -7.51) * mm, "end": v(-118.34, -7.61) * mm});
            skLineSegment(sketch, "E338", {"start": v(-118.34, -7.61) * mm, "end": v(-117.83, -7.7) * mm});
            skLineSegment(sketch, "E339", {"start": v(-117.83, -7.7) * mm, "end": v(-117.33, -7.8) * mm});
            skLineSegment(sketch, "E340", {"start": v(-117.33, -7.8) * mm, "end": v(-116.82, -7.88) * mm});
            skLineSegment(sketch, "E341", {"start": v(-116.82, -7.88) * mm, "end": v(-116.3, -7.97) * mm});
            skLineSegment(sketch, "E342", {"start": v(-116.3, -7.97) * mm, "end": v(-115.8, -8.05) * mm});
            skLineSegment(sketch, "E343", {"start": v(-115.8, -8.05) * mm, "end": v(-115.29, -8.13) * mm});
            skLineSegment(sketch, "E344", {"start": v(-115.29, -8.13) * mm, "end": v(-114.78, -8.2) * mm});
            skLineSegment(sketch, "E345", {"start": v(-114.78, -8.2) * mm, "end": v(-114.27, -8.28) * mm});
            skLineSegment(sketch, "E346", {"start": v(-114.27, -8.28) * mm, "end": v(-113.64, -8.36) * mm});
            skLineSegment(sketch, "E347", {"start": v(-113.64, -8.36) * mm, "end": v(-113, -8.45) * mm});
            skLineSegment(sketch, "E348", {"start": v(-113, -8.45) * mm, "end": v(-112.38, -8.52) * mm});
            skLineSegment(sketch, "E349", {"start": v(-112.38, -8.52) * mm, "end": v(-111.75, -8.6) * mm});
            skLineSegment(sketch, "E350", {"start": v(-111.75, -8.6) * mm, "end": v(-111.12, -8.67) * mm});
            skLineSegment(sketch, "E351", {"start": v(-111.12, -8.67) * mm, "end": v(-110.49, -8.74) * mm});
            skLineSegment(sketch, "E352", {"start": v(-110.49, -8.74) * mm, "end": v(-109.86, -8.8) * mm});
            skLineSegment(sketch, "E353", {"start": v(-109.86, -8.8) * mm, "end": v(-109.23, -8.87) * mm});
            skLineSegment(sketch, "E354", {"start": v(-109.23, -8.87) * mm, "end": v(-108.6, -8.93) * mm});
            skLineSegment(sketch, "E355", {"start": v(-108.6, -8.93) * mm, "end": v(-107.97, -8.99) * mm});
            skLineSegment(sketch, "E356", {"start": v(-107.97, -8.99) * mm, "end": v(-107.22, -9.05) * mm});
            skLineSegment(sketch, "E357", {"start": v(-107.22, -9.05) * mm, "end": v(-106.48, -9.11) * mm});
            skLineSegment(sketch, "E358", {"start": v(-106.48, -9.11) * mm, "end": v(-105.73, -9.17) * mm});
            skLineSegment(sketch, "E359", {"start": v(-105.73, -9.17) * mm, "end": v(-104.98, -9.23) * mm});
            skLineSegment(sketch, "E360", {"start": v(-104.98, -9.23) * mm, "end": v(-104.24, -9.28) * mm});
            skLineSegment(sketch, "E361", {"start": v(-104.24, -9.28) * mm, "end": v(-103.5, -9.34) * mm});
            skLineSegment(sketch, "E362", {"start": v(-103.5, -9.34) * mm, "end": v(-102.74, -9.39) * mm});
            skLineSegment(sketch, "E363", {"start": v(-102.74, -9.39) * mm, "end": v(-102, -9.43) * mm});
            skLineSegment(sketch, "E364", {"start": v(-102, -9.43) * mm, "end": v(-101.25, -9.48) * mm});
            skLineSegment(sketch, "E365", {"start": v(-101.25, -9.48) * mm, "end": v(-99.65, -9.57) * mm});
            skLineSegment(sketch, "E366", {"start": v(-99.65, -9.57) * mm, "end": v(-98.8, -9.61) * mm});
            skLineSegment(sketch, "E367", {"start": v(-98.8, -9.61) * mm, "end": v(-97.93, -9.65) * mm});
            skLineSegment(sketch, "E368", {"start": v(-97.93, -9.65) * mm, "end": v(-97.08, -9.7) * mm});
            skLineSegment(sketch, "E369", {"start": v(-97.08, -9.7) * mm, "end": v(-96.22, -9.73) * mm});
            skLineSegment(sketch, "E370", {"start": v(-96.22, -9.73) * mm, "end": v(-95.36, -9.76) * mm});
            skLineSegment(sketch, "E371", {"start": v(-95.36, -9.76) * mm, "end": v(-94.5, -9.8) * mm});
            skLineSegment(sketch, "E372", {"start": v(-94.5, -9.8) * mm, "end": v(-93.65, -9.82) * mm});
            skLineSegment(sketch, "E373", {"start": v(-93.65, -9.82) * mm, "end": v(-92.8, -9.85) * mm});
            skLineSegment(sketch, "E374", {"start": v(-92.8, -9.85) * mm, "end": v(-91.93, -9.88) * mm});
            skLineSegment(sketch, "E375", {"start": v(-91.93, -9.88) * mm, "end": v(-90.97, -9.9) * mm});
            skLineSegment(sketch, "E376", {"start": v(-90.97, -9.9) * mm, "end": v(-90.01, -9.93) * mm});
            skLineSegment(sketch, "E377", {"start": v(-90.01, -9.93) * mm, "end": v(-89.05, -9.95) * mm});
            skLineSegment(sketch, "E378", {"start": v(-89.05, -9.95) * mm, "end": v(-88.09, -9.98) * mm});
            skLineSegment(sketch, "E379", {"start": v(-88.09, -9.98) * mm, "end": v(-87.13, -10) * mm});
            skLineSegment(sketch, "E380", {"start": v(-87.13, -10) * mm, "end": v(-86.17, -10.01) * mm});
            skLineSegment(sketch, "E381", {"start": v(-86.17, -10.01) * mm, "end": v(-85.2, -10.03) * mm});
            skLineSegment(sketch, "E382", {"start": v(-85.2, -10.03) * mm, "end": v(-84.25, -10.05) * mm});
            skLineSegment(sketch, "E383", {"start": v(-84.25, -10.05) * mm, "end": v(-83.28, -10.06) * mm});
            skLineSegment(sketch, "E384", {"start": v(-83.28, -10.06) * mm, "end": v(-81.27, -10.08) * mm});
            skLineSegment(sketch, "E385", {"start": v(-81.27, -10.08) * mm, "end": v(-80.21, -10.1) * mm});
            skLineSegment(sketch, "E386", {"start": v(-80.21, -10.1) * mm, "end": v(-79.16, -10.1) * mm});
            skLineSegment(sketch, "E387", {"start": v(-79.16, -10.1) * mm, "end": v(-78.1, -10.1) * mm});
            skLineSegment(sketch, "E388", {"start": v(-78.1, -10.1) * mm, "end": v(-77.05, -10.11) * mm});
            skLineSegment(sketch, "E389", {"start": v(-77.05, -10.11) * mm, "end": v(-76, -10.12) * mm});
            skLineSegment(sketch, "E390", {"start": v(-76, -10.12) * mm, "end": v(-74.94, -10.12) * mm});
            skLineSegment(sketch, "E391", {"start": v(-74.94, -10.12) * mm, "end": v(-73.89, -10.12) * mm});
            skLineSegment(sketch, "E392", {"start": v(-73.89, -10.12) * mm, "end": v(-72.83, -10.12) * mm});
            skLineSegment(sketch, "E393", {"start": v(-72.83, -10.12) * mm, "end": v(-71.78, -10.12) * mm});
            skLineSegment(sketch, "E394", {"start": v(-71.78, -10.12) * mm, "end": v(-70.64, -10.11) * mm});
            skLineSegment(sketch, "E395", {"start": v(-70.64, -10.11) * mm, "end": v(-69.5, -10.1) * mm});
            skLineSegment(sketch, "E396", {"start": v(-69.5, -10.1) * mm, "end": v(-68.36, -10.1) * mm});
            skLineSegment(sketch, "E397", {"start": v(-68.36, -10.1) * mm, "end": v(-67.22, -10.1) * mm});
            skLineSegment(sketch, "E398", {"start": v(-67.22, -10.1) * mm, "end": v(-66.08, -10.09) * mm});
            skLineSegment(sketch, "E399", {"start": v(-66.08, -10.09) * mm, "end": v(-64.94, -10.08) * mm});
            skLineSegment(sketch, "E400", {"start": v(-64.94, -10.08) * mm, "end": v(-63.8, -10.07) * mm});
            skLineSegment(sketch, "E401", {"start": v(-63.8, -10.07) * mm, "end": v(-62.67, -10.05) * mm});
            skLineSegment(sketch, "E402", {"start": v(-62.67, -10.05) * mm, "end": v(-61.53, -10.04) * mm});
            skLineSegment(sketch, "E403", {"start": v(-61.53, -10.04) * mm, "end": v(-60.4, -10.03) * mm});
            skLineSegment(sketch, "E404", {"start": v(-60.4, -10.03) * mm, "end": v(-59.18, -10.01) * mm});
            skLineSegment(sketch, "E405", {"start": v(-59.18, -10.01) * mm, "end": v(-57.97, -10) * mm});
            skLineSegment(sketch, "E406", {"start": v(-57.97, -10) * mm, "end": v(-56.76, -9.97) * mm});
            skLineSegment(sketch, "E407", {"start": v(-56.76, -9.97) * mm, "end": v(-55.55, -9.96) * mm});
            skLineSegment(sketch, "E408", {"start": v(-55.55, -9.96) * mm, "end": v(-54.34, -9.93) * mm});
            skLineSegment(sketch, "E409", {"start": v(-54.34, -9.93) * mm, "end": v(-53.14, -9.91) * mm});
            skLineSegment(sketch, "E410", {"start": v(-53.14, -9.91) * mm, "end": v(-51.93, -9.9) * mm});
            skLineSegment(sketch, "E411", {"start": v(-51.93, -9.9) * mm, "end": v(-50.72, -9.87) * mm});
            skLineSegment(sketch, "E412", {"start": v(-50.72, -9.87) * mm, "end": v(-49.5, -9.84) * mm});
            skLineSegment(sketch, "E413", {"start": v(-49.5, -9.84) * mm, "end": v(-47.03, -9.8) * mm});
            skLineSegment(sketch, "E414", {"start": v(-47.03, -9.8) * mm, "end": v(-45.76, -9.76) * mm});
            skLineSegment(sketch, "E415", {"start": v(-45.76, -9.76) * mm, "end": v(-44.5, -9.74) * mm});
            skLineSegment(sketch, "E416", {"start": v(-44.5, -9.74) * mm, "end": v(-43.23, -9.7) * mm});
            skLineSegment(sketch, "E417", {"start": v(-43.23, -9.7) * mm, "end": v(-41.96, -9.68) * mm});
            skLineSegment(sketch, "E418", {"start": v(-41.96, -9.68) * mm, "end": v(-40.7, -9.64) * mm});
            skLineSegment(sketch, "E419", {"start": v(-40.7, -9.64) * mm, "end": v(-39.43, -9.61) * mm});
            skLineSegment(sketch, "E420", {"start": v(-39.43, -9.61) * mm, "end": v(-38.16, -9.58) * mm});
            skLineSegment(sketch, "E421", {"start": v(-38.16, -9.58) * mm, "end": v(-36.9, -9.55) * mm});
            skLineSegment(sketch, "E422", {"start": v(-36.9, -9.55) * mm, "end": v(-34.31, -9.48) * mm});
            skLineSegment(sketch, "E423", {"start": v(-34.31, -9.48) * mm, "end": v(-33, -9.44) * mm});
            skLineSegment(sketch, "E424", {"start": v(-33, -9.44) * mm, "end": v(-31.7, -9.4) * mm});
            skLineSegment(sketch, "E425", {"start": v(-31.7, -9.4) * mm, "end": v(-30.38, -9.37) * mm});
            skLineSegment(sketch, "E426", {"start": v(-30.38, -9.37) * mm, "end": v(-29.07, -9.33) * mm});
            skLineSegment(sketch, "E427", {"start": v(-29.07, -9.33) * mm, "end": v(-27.76, -9.29) * mm});
            skLineSegment(sketch, "E428", {"start": v(-27.76, -9.29) * mm, "end": v(-26.45, -9.25) * mm});
            skLineSegment(sketch, "E429", {"start": v(-26.45, -9.25) * mm, "end": v(-25.13, -9.2) * mm});
            skLineSegment(sketch, "E430", {"start": v(-25.13, -9.2) * mm, "end": v(-23.82, -9.17) * mm});
            skLineSegment(sketch, "E431", {"start": v(-23.82, -9.17) * mm, "end": v(-22.51, -9.13) * mm});
            skLineSegment(sketch, "E432", {"start": v(-22.51, -9.13) * mm, "end": v(-21.17, -9.08) * mm});
            skLineSegment(sketch, "E433", {"start": v(-21.17, -9.08) * mm, "end": v(-19.83, -9.04) * mm});
            skLineSegment(sketch, "E434", {"start": v(-19.83, -9.04) * mm, "end": v(-18.49, -9) * mm});
            skLineSegment(sketch, "E435", {"start": v(-18.49, -9) * mm, "end": v(-17.15, -8.95) * mm});
            skLineSegment(sketch, "E436", {"start": v(-17.15, -8.95) * mm, "end": v(-15.8, -8.9) * mm});
            skLineSegment(sketch, "E437", {"start": v(-15.8, -8.9) * mm, "end": v(-14.47, -8.86) * mm});
            skLineSegment(sketch, "E438", {"start": v(-14.47, -8.86) * mm, "end": v(-13.13, -8.81) * mm});
            skLineSegment(sketch, "E439", {"start": v(-13.13, -8.81) * mm, "end": v(-11.79, -8.77) * mm});
            skLineSegment(sketch, "E440", {"start": v(-11.79, -8.77) * mm, "end": v(-10.44, -8.72) * mm});
            skLineSegment(sketch, "E441", {"start": v(-10.44, -8.72) * mm, "end": v(-7.75, -8.62) * mm});
            skLineSegment(sketch, "E442", {"start": v(-7.75, -8.62) * mm, "end": v(-6.4, -8.57) * mm});
            skLineSegment(sketch, "E443", {"start": v(-6.4, -8.57) * mm, "end": v(-5.04, -8.52) * mm});
            skLineSegment(sketch, "E444", {"start": v(-5.04, -8.52) * mm, "end": v(-3.68, -8.47) * mm});
            skLineSegment(sketch, "E445", {"start": v(-3.68, -8.47) * mm, "end": v(-2.33, -8.42) * mm});
            skLineSegment(sketch, "E446", {"start": v(-2.33, -8.42) * mm, "end": v(-0.97, -8.37) * mm});
            skLineSegment(sketch, "E447", {"start": v(-0.97, -8.37) * mm, "end": v(0.38, -8.32) * mm});
            skLineSegment(sketch, "E448", {"start": v(0.38, -8.32) * mm, "end": v(1.74, -8.27) * mm});
            skLineSegment(sketch, "E449", {"start": v(1.74, -8.27) * mm, "end": v(3.1, -8.22) * mm});
            skLineSegment(sketch, "E450", {"start": v(3.1, -8.22) * mm, "end": v(4.45, -8.17) * mm});
            skLineSegment(sketch, "E451", {"start": v(4.45, -8.17) * mm, "end": v(5.8, -8.12) * mm});
            skLineSegment(sketch, "E452", {"start": v(5.8, -8.12) * mm, "end": v(7.16, -8.06) * mm});
            skLineSegment(sketch, "E453", {"start": v(7.16, -8.06) * mm, "end": v(8.5, -8.01) * mm});
            skLineSegment(sketch, "E454", {"start": v(8.5, -8.01) * mm, "end": v(9.86, -7.96) * mm});
            skLineSegment(sketch, "E455", {"start": v(9.86, -7.96) * mm, "end": v(11.22, -7.9) * mm});
            skLineSegment(sketch, "E456", {"start": v(11.22, -7.9) * mm, "end": v(12.57, -7.85) * mm});
            skLineSegment(sketch, "E457", {"start": v(12.57, -7.85) * mm, "end": v(13.93, -7.8) * mm});
            skLineSegment(sketch, "E458", {"start": v(13.93, -7.8) * mm, "end": v(15.28, -7.75) * mm});
            skLineSegment(sketch, "E459", {"start": v(15.28, -7.75) * mm, "end": v(16.63, -7.7) * mm});
            skLineSegment(sketch, "E460", {"start": v(16.63, -7.7) * mm, "end": v(17.99, -7.64) * mm});
            skLineSegment(sketch, "E461", {"start": v(17.99, -7.64) * mm, "end": v(19.33, -7.58) * mm});
            skLineSegment(sketch, "E462", {"start": v(19.33, -7.58) * mm, "end": v(20.66, -7.53) * mm});
            skLineSegment(sketch, "E463", {"start": v(20.66, -7.53) * mm, "end": v(22, -7.47) * mm});
            skLineSegment(sketch, "E464", {"start": v(22, -7.47) * mm, "end": v(23.34, -7.42) * mm});
            skLineSegment(sketch, "E465", {"start": v(23.34, -7.42) * mm, "end": v(24.68, -7.37) * mm});
            skLineSegment(sketch, "E466", {"start": v(24.68, -7.37) * mm, "end": v(26.01, -7.31) * mm});
            skLineSegment(sketch, "E467", {"start": v(26.01, -7.31) * mm, "end": v(27.35, -7.26) * mm});
            skLineSegment(sketch, "E468", {"start": v(27.35, -7.26) * mm, "end": v(28.69, -7.2) * mm});
            skLineSegment(sketch, "E469", {"start": v(28.69, -7.2) * mm, "end": v(30.03, -7.15) * mm});
            skLineSegment(sketch, "E470", {"start": v(30.03, -7.15) * mm, "end": v(32.67, -7.04) * mm});
            skLineSegment(sketch, "E471", {"start": v(32.67, -7.04) * mm, "end": v(33.98, -6.98) * mm});
            skLineSegment(sketch, "E472", {"start": v(33.98, -6.98) * mm, "end": v(35.28, -6.93) * mm});
            skLineSegment(sketch, "E473", {"start": v(35.28, -6.93) * mm, "end": v(36.59, -6.88) * mm});
            skLineSegment(sketch, "E474", {"start": v(36.59, -6.88) * mm, "end": v(37.9, -6.82) * mm});
            skLineSegment(sketch, "E475", {"start": v(37.9, -6.82) * mm, "end": v(39.2, -6.77) * mm});
            skLineSegment(sketch, "E476", {"start": v(39.2, -6.77) * mm, "end": v(40.5, -6.72) * mm});
            skLineSegment(sketch, "E477", {"start": v(40.5, -6.72) * mm, "end": v(41.81, -6.66) * mm});
            skLineSegment(sketch, "E478", {"start": v(41.81, -6.66) * mm, "end": v(43.12, -6.6) * mm});
            skLineSegment(sketch, "E479", {"start": v(43.12, -6.6) * mm, "end": v(45.68, -6.5) * mm});
            skLineSegment(sketch, "E480", {"start": v(45.68, -6.5) * mm, "end": v(46.94, -6.45) * mm});
            skLineSegment(sketch, "E481", {"start": v(46.94, -6.45) * mm, "end": v(48.2, -6.4) * mm});
            skLineSegment(sketch, "E482", {"start": v(48.2, -6.4) * mm, "end": v(49.46, -6.35) * mm});
            skLineSegment(sketch, "E483", {"start": v(49.46, -6.35) * mm, "end": v(50.71, -6.3) * mm});
            skLineSegment(sketch, "E484", {"start": v(50.71, -6.3) * mm, "end": v(51.97, -6.25) * mm});
            skLineSegment(sketch, "E485", {"start": v(51.97, -6.25) * mm, "end": v(53.23, -6.2) * mm});
            skLineSegment(sketch, "E486", {"start": v(53.23, -6.2) * mm, "end": v(54.49, -6.14) * mm});
            skLineSegment(sketch, "E487", {"start": v(54.49, -6.14) * mm, "end": v(55.75, -6.1) * mm});
            skLineSegment(sketch, "E488", {"start": v(55.75, -6.1) * mm, "end": v(57, -6.04) * mm});
            skLineSegment(sketch, "E489", {"start": v(57, -6.04) * mm, "end": v(58.2, -6) * mm});
            skLineSegment(sketch, "E490", {"start": v(58.2, -6) * mm, "end": v(59.4, -5.95) * mm});
            skLineSegment(sketch, "E491", {"start": v(59.4, -5.95) * mm, "end": v(60.6, -5.9) * mm});
            skLineSegment(sketch, "E492", {"start": v(60.6, -5.9) * mm, "end": v(61.79, -5.85) * mm});
            skLineSegment(sketch, "E493", {"start": v(61.79, -5.85) * mm, "end": v(62.98, -5.8) * mm});
            skLineSegment(sketch, "E494", {"start": v(62.98, -5.8) * mm, "end": v(64.18, -5.75) * mm});
            skLineSegment(sketch, "E495", {"start": v(64.18, -5.75) * mm, "end": v(65.38, -5.7) * mm});
            skLineSegment(sketch, "E496", {"start": v(65.38, -5.7) * mm, "end": v(66.57, -5.66) * mm});
            skLineSegment(sketch, "E497", {"start": v(66.57, -5.66) * mm, "end": v(67.77, -5.61) * mm});
            skLineSegment(sketch, "E498", {"start": v(67.77, -5.61) * mm, "end": v(68.96, -5.57) * mm});
            skLineSegment(sketch, "E499", {"start": v(68.96, -5.57) * mm, "end": v(70.08, -5.52) * mm});
            skLineSegment(sketch, "E500", {"start": v(70.08, -5.52) * mm, "end": v(71.2, -5.48) * mm});
            skLineSegment(sketch, "E501", {"start": v(71.2, -5.48) * mm, "end": v(72.32, -5.44) * mm});
            skLineSegment(sketch, "E502", {"start": v(72.32, -5.44) * mm, "end": v(73.44, -5.4) * mm});
            skLineSegment(sketch, "E503", {"start": v(73.44, -5.4) * mm, "end": v(74.56, -5.35) * mm});
            skLineSegment(sketch, "E504", {"start": v(74.56, -5.35) * mm, "end": v(75.68, -5.31) * mm});
            skLineSegment(sketch, "E505", {"start": v(75.68, -5.31) * mm, "end": v(76.8, -5.27) * mm});
            skLineSegment(sketch, "E506", {"start": v(76.8, -5.27) * mm, "end": v(77.91, -5.23) * mm});
            skLineSegment(sketch, "E507", {"start": v(77.91, -5.23) * mm, "end": v(79.03, -5.19) * mm});
            skLineSegment(sketch, "E508", {"start": v(79.03, -5.19) * mm, "end": v(81.18, -5.1) * mm});
            skLineSegment(sketch, "E509", {"start": v(81.18, -5.1) * mm, "end": v(82.2, -5.07) * mm});
            skLineSegment(sketch, "E510", {"start": v(82.2, -5.07) * mm, "end": v(83.23, -5.03) * mm});
            skLineSegment(sketch, "E511", {"start": v(83.23, -5.03) * mm, "end": v(84.26, -5) * mm});
            skLineSegment(sketch, "E512", {"start": v(84.26, -5) * mm, "end": v(85.29, -4.96) * mm});
            skLineSegment(sketch, "E513", {"start": v(85.29, -4.96) * mm, "end": v(86.31, -4.93) * mm});
            skLineSegment(sketch, "E514", {"start": v(86.31, -4.93) * mm, "end": v(87.34, -4.9) * mm});
            skLineSegment(sketch, "E515", {"start": v(87.34, -4.9) * mm, "end": v(88.37, -4.86) * mm});
            skLineSegment(sketch, "E516", {"start": v(88.37, -4.86) * mm, "end": v(89.4, -4.82) * mm});
            skLineSegment(sketch, "E517", {"start": v(89.4, -4.82) * mm, "end": v(90.42, -4.79) * mm});
            skLineSegment(sketch, "E518", {"start": v(90.42, -4.79) * mm, "end": v(91.34, -4.76) * mm});
            skLineSegment(sketch, "E519", {"start": v(91.34, -4.76) * mm, "end": v(92.27, -4.73) * mm});
            skLineSegment(sketch, "E520", {"start": v(92.27, -4.73) * mm, "end": v(93.19, -4.7) * mm});
            skLineSegment(sketch, "E521", {"start": v(93.19, -4.7) * mm, "end": v(94.11, -4.67) * mm});
            skLineSegment(sketch, "E522", {"start": v(94.11, -4.67) * mm, "end": v(95.03, -4.64) * mm});
            skLineSegment(sketch, "E523", {"start": v(95.03, -4.64) * mm, "end": v(95.96, -4.61) * mm});
            skLineSegment(sketch, "E524", {"start": v(95.96, -4.61) * mm, "end": v(96.88, -4.59) * mm});
            skLineSegment(sketch, "E525", {"start": v(96.88, -4.59) * mm, "end": v(97.8, -4.56) * mm});
            skLineSegment(sketch, "E526", {"start": v(97.8, -4.56) * mm, "end": v(98.72, -4.53) * mm});
            skLineSegment(sketch, "E527", {"start": v(98.72, -4.53) * mm, "end": v(99.64, -4.5) * mm});
            skLineSegment(sketch, "E528", {"start": v(99.64, -4.5) * mm, "end": v(100.45, -4.48) * mm});
            skLineSegment(sketch, "E529", {"start": v(100.45, -4.48) * mm, "end": v(101.25, -4.46) * mm});
            skLineSegment(sketch, "E530", {"start": v(101.25, -4.46) * mm, "end": v(102.06, -4.44) * mm});
            skLineSegment(sketch, "E531", {"start": v(102.06, -4.44) * mm, "end": v(102.86, -4.42) * mm});
            skLineSegment(sketch, "E532", {"start": v(102.86, -4.42) * mm, "end": v(103.67, -4.4) * mm});
            skLineSegment(sketch, "E533", {"start": v(103.67, -4.4) * mm, "end": v(104.47, -4.37) * mm});
            skLineSegment(sketch, "E534", {"start": v(104.47, -4.37) * mm, "end": v(105.28, -4.35) * mm});
            skLineSegment(sketch, "E535", {"start": v(105.28, -4.35) * mm, "end": v(106.08, -4.33) * mm});
            skLineSegment(sketch, "E536", {"start": v(106.08, -4.33) * mm, "end": v(106.89, -4.31) * mm});
            skLineSegment(sketch, "E537", {"start": v(106.89, -4.31) * mm, "end": v(107.7, -4.3) * mm});
            skLineSegment(sketch, "E538", {"start": v(107.7, -4.3) * mm, "end": v(108.37, -4.28) * mm});
            skLineSegment(sketch, "E539", {"start": v(108.37, -4.28) * mm, "end": v(109.05, -4.26) * mm});
            skLineSegment(sketch, "E540", {"start": v(109.05, -4.26) * mm, "end": v(109.72, -4.25) * mm});
            skLineSegment(sketch, "E541", {"start": v(109.72, -4.25) * mm, "end": v(110.4, -4.23) * mm});
            skLineSegment(sketch, "E542", {"start": v(110.4, -4.23) * mm, "end": v(111.08, -4.22) * mm});
            skLineSegment(sketch, "E543", {"start": v(111.08, -4.22) * mm, "end": v(111.75, -4.2) * mm});
            skLineSegment(sketch, "E544", {"start": v(111.75, -4.2) * mm, "end": v(112.43, -4.19) * mm});
            skLineSegment(sketch, "E545", {"start": v(112.43, -4.19) * mm, "end": v(113.1, -4.17) * mm});
            skLineSegment(sketch, "E546", {"start": v(113.1, -4.17) * mm, "end": v(113.78, -4.16) * mm});
            skLineSegment(sketch, "E547", {"start": v(113.78, -4.16) * mm, "end": v(115, -4.14) * mm});
            skLineSegment(sketch, "E548", {"start": v(115, -4.14) * mm, "end": v(115.53, -4.13) * mm});
            skLineSegment(sketch, "E549", {"start": v(115.53, -4.13) * mm, "end": v(116.07, -4.12) * mm});
            skLineSegment(sketch, "E550", {"start": v(116.07, -4.12) * mm, "end": v(116.6, -4.1) * mm});
            skLineSegment(sketch, "E551", {"start": v(116.6, -4.1) * mm, "end": v(117.15, -4.1) * mm});
            skLineSegment(sketch, "E552", {"start": v(117.15, -4.1) * mm, "end": v(117.69, -4.09) * mm});
            skLineSegment(sketch, "E553", {"start": v(117.69, -4.09) * mm, "end": v(118.22, -4.08) * mm});
            skLineSegment(sketch, "E554", {"start": v(118.22, -4.08) * mm, "end": v(118.76, -4.07) * mm});
            skLineSegment(sketch, "E555", {"start": v(118.76, -4.07) * mm, "end": v(119.3, -4.06) * mm});
            skLineSegment(sketch, "E556", {"start": v(119.3, -4.06) * mm, "end": v(119.84, -4.05) * mm});
            skLineSegment(sketch, "E557", {"start": v(119.84, -4.05) * mm, "end": v(124, -3.99) * mm});
            skLineSegment(sketch, "E558", {"start": v(124, -3.99) * mm, "end": v(124.24, -3.99) * mm});
            skLineSegment(sketch, "E559", {"start": v(124.24, -3.99) * mm, "end": v(124.48, -3.98) * mm});
            skLineSegment(sketch, "E560", {"start": v(124.48, -3.98) * mm, "end": v(124.73, -3.98) * mm});
            skLineSegment(sketch, "E561", {"start": v(124.73, -3.98) * mm, "end": v(124.97, -3.98) * mm});
            skLineSegment(sketch, "E562", {"start": v(124.97, -3.98) * mm, "end": v(125.2, -3.97) * mm});
            skLineSegment(sketch, "E563", {"start": v(125.2, -3.97) * mm, "end": v(125.45, -3.97) * mm});
            skLineSegment(sketch, "E564", {"start": v(125.45, -3.97) * mm, "end": v(125.7, -3.97) * mm});
            skLineSegment(sketch, "E565", {"start": v(125.7, -3.97) * mm, "end": v(125.93, -3.96) * mm});
            skLineSegment(sketch, "E566", {"start": v(125.93, -3.96) * mm, "end": v(126.17, -3.96) * mm});
            skLineSegment(sketch, "E567", {"start": v(126.17, -3.96) * mm, "end": v(126.26, -3.96) * mm});
            skLineSegment(sketch, "E568", {"start": v(126.26, -3.96) * mm, "end": v(126.34, -3.96) * mm});
            skLineSegment(sketch, "E569", {"start": v(126.34, -3.96) * mm, "end": v(126.42, -3.96) * mm});
            skLineSegment(sketch, "E570", {"start": v(126.42, -3.96) * mm, "end": v(126.5, -3.96) * mm});
            skLineSegment(sketch, "E571", {"start": v(126.5, -3.96) * mm, "end": v(126.59, -3.96) * mm});
            skLineSegment(sketch, "E572", {"start": v(126.59, -3.96) * mm, "end": v(126.67, -3.96) * mm});
            skLineSegment(sketch, "E573", {"start": v(126.67, -3.96) * mm, "end": v(126.75, -3.96) * mm});
            skLineSegment(sketch, "E574", {"start": v(126.75, -3.96) * mm, "end": v(126.83, -3.96) * mm});
            skLineSegment(sketch, "E575", {"start": v(126.83, -3.96) * mm, "end": v(126.92, -3.95) * mm});
            skLineSegment(sketch, "E576", {"start": v(126.92, -3.95) * mm, "end": v(127, -3.95) * mm});
            skLineSegment(sketch, "E577", {"start": v(61.39, 2.74) * mm, "end": v(60.75, 2.81) * mm});
            skLineSegment(sketch, "E578", {"start": v(60.75, 2.81) * mm, "end": v(60.12, 2.88) * mm});
            skLineSegment(sketch, "E579", {"start": v(60.12, 2.88) * mm, "end": v(59.48, 2.95) * mm});
            skLineSegment(sketch, "E580", {"start": v(59.48, 2.95) * mm, "end": v(58.85, 3.02) * mm});
            skLineSegment(sketch, "E581", {"start": v(58.85, 3.02) * mm, "end": v(58.21, 3.08) * mm});
            skLineSegment(sketch, "E582", {"start": v(58.21, 3.08) * mm, "end": v(57.58, 3.15) * mm});
            skLineSegment(sketch, "E583", {"start": v(57.58, 3.15) * mm, "end": v(56.94, 3.22) * mm});
            skLineSegment(sketch, "E584", {"start": v(56.94, 3.22) * mm, "end": v(56.3, 3.28) * mm});
            skLineSegment(sketch, "E585", {"start": v(56.3, 3.28) * mm, "end": v(55.67, 3.35) * mm});
            skLineSegment(sketch, "E586", {"start": v(55.67, 3.35) * mm, "end": v(55.04, 3.42) * mm});
            skLineSegment(sketch, "E587", {"start": v(55.04, 3.42) * mm, "end": v(54.4, 3.48) * mm});
            skLineSegment(sketch, "E588", {"start": v(54.4, 3.48) * mm, "end": v(53.77, 3.55) * mm});
            skLineSegment(sketch, "E589", {"start": v(53.77, 3.55) * mm, "end": v(53.13, 3.6) * mm});
            skLineSegment(sketch, "E590", {"start": v(53.13, 3.6) * mm, "end": v(52.5, 3.67) * mm});
            skLineSegment(sketch, "E591", {"start": v(52.5, 3.67) * mm, "end": v(51.86, 3.74) * mm});
            skLineSegment(sketch, "E592", {"start": v(51.86, 3.74) * mm, "end": v(51.23, 3.8) * mm});
            skLineSegment(sketch, "E593", {"start": v(51.23, 3.8) * mm, "end": v(50.6, 3.86) * mm});
            skLineSegment(sketch, "E594", {"start": v(50.6, 3.86) * mm, "end": v(49.96, 3.92) * mm});
            skLineSegment(sketch, "E595", {"start": v(49.96, 3.92) * mm, "end": v(49.32, 3.98) * mm});
            skLineSegment(sketch, "E596", {"start": v(49.32, 3.98) * mm, "end": v(48.69, 4.05) * mm});
            skLineSegment(sketch, "E597", {"start": v(48.69, 4.05) * mm, "end": v(48.05, 4.1) * mm});
            skLineSegment(sketch, "E598", {"start": v(48.05, 4.1) * mm, "end": v(47.42, 4.17) * mm});
            skLineSegment(sketch, "E599", {"start": v(47.42, 4.17) * mm, "end": v(46.78, 4.23) * mm});
            skLineSegment(sketch, "E600", {"start": v(46.78, 4.23) * mm, "end": v(46.14, 4.28) * mm});
            skLineSegment(sketch, "E601", {"start": v(46.14, 4.28) * mm, "end": v(45.5, 4.34) * mm});
            skLineSegment(sketch, "E602", {"start": v(45.5, 4.34) * mm, "end": v(44.87, 4.4) * mm});
            skLineSegment(sketch, "E603", {"start": v(44.87, 4.4) * mm, "end": v(44.24, 4.46) * mm});
            skLineSegment(sketch, "E604", {"start": v(44.24, 4.46) * mm, "end": v(43.6, 4.52) * mm});
            skLineSegment(sketch, "E605", {"start": v(43.6, 4.52) * mm, "end": v(42.97, 4.57) * mm});
            skLineSegment(sketch, "E606", {"start": v(42.97, 4.57) * mm, "end": v(42.33, 4.63) * mm});
            skLineSegment(sketch, "E607", {"start": v(42.33, 4.63) * mm, "end": v(41.7, 4.69) * mm});
            skLineSegment(sketch, "E608", {"start": v(41.7, 4.69) * mm, "end": v(41.06, 4.74) * mm});
            skLineSegment(sketch, "E609", {"start": v(41.06, 4.74) * mm, "end": v(40.43, 4.8) * mm});
            skLineSegment(sketch, "E610", {"start": v(40.43, 4.8) * mm, "end": v(39.8, 4.85) * mm});
            skLineSegment(sketch, "E611", {"start": v(39.8, 4.85) * mm, "end": v(39.16, 4.9) * mm});
            skLineSegment(sketch, "E612", {"start": v(39.16, 4.9) * mm, "end": v(38.52, 4.96) * mm});
            skLineSegment(sketch, "E613", {"start": v(38.52, 4.96) * mm, "end": v(37.89, 5.02) * mm});
            skLineSegment(sketch, "E614", {"start": v(37.89, 5.02) * mm, "end": v(37.25, 5.07) * mm});
            skLineSegment(sketch, "E615", {"start": v(37.25, 5.07) * mm, "end": v(36.62, 5.12) * mm});
            skLineSegment(sketch, "E616", {"start": v(36.62, 5.12) * mm, "end": v(35.98, 5.18) * mm});
            skLineSegment(sketch, "E617", {"start": v(35.98, 5.18) * mm, "end": v(35.35, 5.23) * mm});
            skLineSegment(sketch, "E618", {"start": v(35.35, 5.23) * mm, "end": v(34.71, 5.28) * mm});
            skLineSegment(sketch, "E619", {"start": v(34.71, 5.28) * mm, "end": v(34.08, 5.33) * mm});
            skLineSegment(sketch, "E620", {"start": v(34.08, 5.33) * mm, "end": v(33.44, 5.38) * mm});
            skLineSegment(sketch, "E621", {"start": v(33.44, 5.38) * mm, "end": v(32.8, 5.43) * mm});
            skLineSegment(sketch, "E622", {"start": v(32.8, 5.43) * mm, "end": v(32.17, 5.48) * mm});
            skLineSegment(sketch, "E623", {"start": v(32.17, 5.48) * mm, "end": v(31.54, 5.53) * mm});
            skLineSegment(sketch, "E624", {"start": v(31.54, 5.53) * mm, "end": v(30.9, 5.58) * mm});
            skLineSegment(sketch, "E625", {"start": v(30.9, 5.58) * mm, "end": v(30.27, 5.63) * mm});
            skLineSegment(sketch, "E626", {"start": v(30.27, 5.63) * mm, "end": v(29.63, 5.68) * mm});
            skLineSegment(sketch, "E627", {"start": v(29.63, 5.68) * mm, "end": v(29, 5.73) * mm});
            skLineSegment(sketch, "E628", {"start": v(29, 5.73) * mm, "end": v(28.36, 5.78) * mm});
            skLineSegment(sketch, "E629", {"start": v(28.36, 5.78) * mm, "end": v(27.73, 5.82) * mm});
            skLineSegment(sketch, "E630", {"start": v(27.73, 5.82) * mm, "end": v(27.1, 5.87) * mm});
            skLineSegment(sketch, "E631", {"start": v(27.1, 5.87) * mm, "end": v(26.46, 5.92) * mm});
            skLineSegment(sketch, "E632", {"start": v(26.46, 5.92) * mm, "end": v(25.82, 5.96) * mm});
            skLineSegment(sketch, "E633", {"start": v(25.82, 5.96) * mm, "end": v(25.19, 6.01) * mm});
            skLineSegment(sketch, "E634", {"start": v(25.19, 6.01) * mm, "end": v(24.55, 6.06) * mm});
            skLineSegment(sketch, "E635", {"start": v(24.55, 6.06) * mm, "end": v(23.92, 6.1) * mm});
            skLineSegment(sketch, "E636", {"start": v(23.92, 6.1) * mm, "end": v(23.28, 6.15) * mm});
            skLineSegment(sketch, "E637", {"start": v(23.28, 6.15) * mm, "end": v(22.65, 6.2) * mm});
            skLineSegment(sketch, "E638", {"start": v(22.65, 6.2) * mm, "end": v(22, 6.24) * mm});
            skLineSegment(sketch, "E639", {"start": v(22, 6.24) * mm, "end": v(21.37, 6.28) * mm});
            skLineSegment(sketch, "E640", {"start": v(21.37, 6.28) * mm, "end": v(20.74, 6.32) * mm});
            skLineSegment(sketch, "E641", {"start": v(20.74, 6.32) * mm, "end": v(20.1, 6.37) * mm});
            skLineSegment(sketch, "E642", {"start": v(20.1, 6.37) * mm, "end": v(19.47, 6.4) * mm});
            skLineSegment(sketch, "E643", {"start": v(19.47, 6.4) * mm, "end": v(18.83, 6.45) * mm});
            skLineSegment(sketch, "E644", {"start": v(18.83, 6.45) * mm, "end": v(18.2, 6.5) * mm});
            skLineSegment(sketch, "E645", {"start": v(18.2, 6.5) * mm, "end": v(17.56, 6.53) * mm});
            skLineSegment(sketch, "E646", {"start": v(17.56, 6.53) * mm, "end": v(16.93, 6.58) * mm});
            skLineSegment(sketch, "E647", {"start": v(16.93, 6.58) * mm, "end": v(16.3, 6.62) * mm});
            skLineSegment(sketch, "E648", {"start": v(16.3, 6.62) * mm, "end": v(15.66, 6.66) * mm});
            skLineSegment(sketch, "E649", {"start": v(15.66, 6.66) * mm, "end": v(15.02, 6.7) * mm});
            skLineSegment(sketch, "E650", {"start": v(15.02, 6.7) * mm, "end": v(14.39, 6.74) * mm});
            skLineSegment(sketch, "E651", {"start": v(14.39, 6.74) * mm, "end": v(13.75, 6.78) * mm});
            skLineSegment(sketch, "E652", {"start": v(13.75, 6.78) * mm, "end": v(13.12, 6.82) * mm});
            skLineSegment(sketch, "E653", {"start": v(13.12, 6.82) * mm, "end": v(12.48, 6.85) * mm});
            skLineSegment(sketch, "E654", {"start": v(12.48, 6.85) * mm, "end": v(11.85, 6.9) * mm});
            skLineSegment(sketch, "E655", {"start": v(11.85, 6.9) * mm, "end": v(11.21, 6.93) * mm});
            skLineSegment(sketch, "E656", {"start": v(11.21, 6.93) * mm, "end": v(10.58, 6.97) * mm});
            skLineSegment(sketch, "E657", {"start": v(10.58, 6.97) * mm, "end": v(9.94, 7) * mm});
            skLineSegment(sketch, "E658", {"start": v(9.94, 7) * mm, "end": v(9.3, 7.04) * mm});
            skLineSegment(sketch, "E659", {"start": v(9.3, 7.04) * mm, "end": v(8.67, 7.08) * mm});
            skLineSegment(sketch, "E660", {"start": v(8.67, 7.08) * mm, "end": v(8.04, 7.12) * mm});
            skLineSegment(sketch, "E661", {"start": v(8.04, 7.12) * mm, "end": v(7.4, 7.15) * mm});
            skLineSegment(sketch, "E662", {"start": v(7.4, 7.15) * mm, "end": v(6.77, 7.19) * mm});
            skLineSegment(sketch, "E663", {"start": v(6.77, 7.19) * mm, "end": v(6.13, 7.22) * mm});
            skLineSegment(sketch, "E664", {"start": v(6.13, 7.22) * mm, "end": v(5.5, 7.26) * mm});
            skLineSegment(sketch, "E665", {"start": v(5.5, 7.26) * mm, "end": v(4.86, 7.3) * mm});
            skLineSegment(sketch, "E666", {"start": v(4.86, 7.3) * mm, "end": v(4.23, 7.33) * mm});
            skLineSegment(sketch, "E667", {"start": v(4.23, 7.33) * mm, "end": v(3.6, 7.36) * mm});
            skLineSegment(sketch, "E668", {"start": v(3.6, 7.36) * mm, "end": v(2.96, 7.4) * mm});
            skLineSegment(sketch, "E669", {"start": v(2.96, 7.4) * mm, "end": v(2.32, 7.43) * mm});
            skLineSegment(sketch, "E670", {"start": v(2.32, 7.43) * mm, "end": v(1.69, 7.46) * mm});
            skLineSegment(sketch, "E671", {"start": v(1.69, 7.46) * mm, "end": v(1.05, 7.5) * mm});
            skLineSegment(sketch, "E672", {"start": v(1.05, 7.5) * mm, "end": v(0.42, 7.53) * mm});
            skLineSegment(sketch, "E673", {"start": v(0.42, 7.53) * mm, "end": v(-0.22, 7.56) * mm});
            skLineSegment(sketch, "E674", {"start": v(-0.22, 7.56) * mm, "end": v(-0.85, 7.59) * mm});
            skLineSegment(sketch, "E675", {"start": v(-0.85, 7.59) * mm, "end": v(-1.49, 7.62) * mm});
            skLineSegment(sketch, "E676", {"start": v(-1.49, 7.62) * mm, "end": v(-2.12, 7.65) * mm});
            skLineSegment(sketch, "E677", {"start": v(-2.12, 7.65) * mm, "end": v(-2.76, 7.68) * mm});
            skLineSegment(sketch, "E678", {"start": v(-2.76, 7.68) * mm, "end": v(-3.4, 7.7) * mm});
            skLineSegment(sketch, "E679", {"start": v(-3.4, 7.7) * mm, "end": v(-4.03, 7.74) * mm});
            skLineSegment(sketch, "E680", {"start": v(-4.03, 7.74) * mm, "end": v(-4.67, 7.77) * mm});
            skLineSegment(sketch, "E681", {"start": v(-4.67, 7.77) * mm, "end": v(-5.3, 7.8) * mm});
            skLineSegment(sketch, "E682", {"start": v(-5.3, 7.8) * mm, "end": v(-5.94, 7.82) * mm});
            skLineSegment(sketch, "E683", {"start": v(-5.94, 7.82) * mm, "end": v(-6.57, 7.85) * mm});
            skLineSegment(sketch, "E684", {"start": v(-6.57, 7.85) * mm, "end": v(-7.2, 7.88) * mm});
            skLineSegment(sketch, "E685", {"start": v(-7.2, 7.88) * mm, "end": v(-7.84, 7.9) * mm});
            skLineSegment(sketch, "E686", {"start": v(-7.84, 7.9) * mm, "end": v(-8.48, 7.93) * mm});
            skLineSegment(sketch, "E687", {"start": v(-8.48, 7.93) * mm, "end": v(-9.11, 7.95) * mm});
            skLineSegment(sketch, "E688", {"start": v(-9.11, 7.95) * mm, "end": v(-9.75, 7.98) * mm});
            skLineSegment(sketch, "E689", {"start": v(-9.75, 7.98) * mm, "end": v(-10.38, 8) * mm});
            skLineSegment(sketch, "E690", {"start": v(-10.38, 8) * mm, "end": v(-11.02, 8.03) * mm});
            skLineSegment(sketch, "E691", {"start": v(-11.02, 8.03) * mm, "end": v(-11.65, 8.05) * mm});
            skLineSegment(sketch, "E692", {"start": v(-11.65, 8.05) * mm, "end": v(-12.29, 8.07) * mm});
            skLineSegment(sketch, "E693", {"start": v(-12.29, 8.07) * mm, "end": v(-12.92, 8.1) * mm});
            skLineSegment(sketch, "E694", {"start": v(-12.92, 8.1) * mm, "end": v(-13.56, 8.12) * mm});
            skLineSegment(sketch, "E695", {"start": v(-13.56, 8.12) * mm, "end": v(-14.2, 8.14) * mm});
            skLineSegment(sketch, "E696", {"start": v(-14.2, 8.14) * mm, "end": v(-14.83, 8.16) * mm});
            skLineSegment(sketch, "E697", {"start": v(-14.83, 8.16) * mm, "end": v(-15.46, 8.18) * mm});
            skLineSegment(sketch, "E698", {"start": v(-15.46, 8.18) * mm, "end": v(-16.1, 8.2) * mm});
            skLineSegment(sketch, "E699", {"start": v(-16.1, 8.2) * mm, "end": v(-16.73, 8.22) * mm});
            skLineSegment(sketch, "E700", {"start": v(-16.73, 8.22) * mm, "end": v(-17.37, 8.24) * mm});
            skLineSegment(sketch, "E701", {"start": v(-17.37, 8.24) * mm, "end": v(-18, 8.26) * mm});
            skLineSegment(sketch, "E702", {"start": v(-18, 8.26) * mm, "end": v(-18.64, 8.28) * mm});
            skLineSegment(sketch, "E703", {"start": v(-18.64, 8.28) * mm, "end": v(-19.27, 8.3) * mm});
            skLineSegment(sketch, "E704", {"start": v(-19.27, 8.3) * mm, "end": v(-19.9, 8.31) * mm});
            skLineSegment(sketch, "E705", {"start": v(-19.9, 8.31) * mm, "end": v(-20.54, 8.33) * mm});
            skLineSegment(sketch, "E706", {"start": v(-20.54, 8.33) * mm, "end": v(-21.18, 8.35) * mm});
            skLineSegment(sketch, "E707", {"start": v(-21.18, 8.35) * mm, "end": v(-21.81, 8.36) * mm});
            skLineSegment(sketch, "E708", {"start": v(-21.81, 8.36) * mm, "end": v(-22.45, 8.38) * mm});
            skLineSegment(sketch, "E709", {"start": v(-22.45, 8.38) * mm, "end": v(-23.08, 8.4) * mm});
            skLineSegment(sketch, "E710", {"start": v(-23.08, 8.4) * mm, "end": v(-23.72, 8.41) * mm});
            skLineSegment(sketch, "E711", {"start": v(-23.72, 8.41) * mm, "end": v(-24.36, 8.42) * mm});
            skLineSegment(sketch, "E712", {"start": v(-24.36, 8.42) * mm, "end": v(-25, 8.44) * mm});
            skLineSegment(sketch, "E713", {"start": v(-25, 8.44) * mm, "end": v(-25.63, 8.45) * mm});
            skLineSegment(sketch, "E714", {"start": v(-25.63, 8.45) * mm, "end": v(-26.26, 8.46) * mm});
            skLineSegment(sketch, "E715", {"start": v(-26.26, 8.46) * mm, "end": v(-26.9, 8.48) * mm});
            skLineSegment(sketch, "E716", {"start": v(-26.9, 8.48) * mm, "end": v(-27.53, 8.49) * mm});
            skLineSegment(sketch, "E717", {"start": v(-27.53, 8.49) * mm, "end": v(-28.17, 8.5) * mm});
            skLineSegment(sketch, "E718", {"start": v(-28.17, 8.5) * mm, "end": v(-28.8, 8.51) * mm});
            skLineSegment(sketch, "E719", {"start": v(-28.8, 8.51) * mm, "end": v(-29.44, 8.52) * mm});
            skLineSegment(sketch, "E720", {"start": v(-29.44, 8.52) * mm, "end": v(-30.07, 8.53) * mm});
            skLineSegment(sketch, "E721", {"start": v(-30.07, 8.53) * mm, "end": v(-30.7, 8.54) * mm});
            skLineSegment(sketch, "E722", {"start": v(-30.7, 8.54) * mm, "end": v(-31.34, 8.55) * mm});
            skLineSegment(sketch, "E723", {"start": v(-31.34, 8.55) * mm, "end": v(-31.98, 8.56) * mm});
            skLineSegment(sketch, "E724", {"start": v(-31.98, 8.56) * mm, "end": v(-32.61, 8.57) * mm});
            skLineSegment(sketch, "E725", {"start": v(-32.61, 8.57) * mm, "end": v(-33.25, 8.57) * mm});
            skLineSegment(sketch, "E726", {"start": v(-33.25, 8.57) * mm, "end": v(-33.88, 8.58) * mm});
            skLineSegment(sketch, "E727", {"start": v(-33.88, 8.58) * mm, "end": v(-34.52, 8.59) * mm});
            skLineSegment(sketch, "E728", {"start": v(-34.52, 8.59) * mm, "end": v(-35.15, 8.6) * mm});
            skLineSegment(sketch, "E729", {"start": v(-35.15, 8.6) * mm, "end": v(-35.79, 8.6) * mm});
            skLineSegment(sketch, "E730", {"start": v(-35.79, 8.6) * mm, "end": v(-36.42, 8.6) * mm});
            skLineSegment(sketch, "E731", {"start": v(-36.42, 8.6) * mm, "end": v(-37.06, 8.6) * mm});
            skLineSegment(sketch, "E732", {"start": v(-37.06, 8.6) * mm, "end": v(-37.7, 8.6) * mm});
            skLineSegment(sketch, "E733", {"start": v(-37.7, 8.6) * mm, "end": v(-38.33, 8.61) * mm});
            skLineSegment(sketch, "E734", {"start": v(-38.33, 8.61) * mm, "end": v(-38.96, 8.62) * mm});
            skLineSegment(sketch, "E735", {"start": v(-38.96, 8.62) * mm, "end": v(-39.6, 8.62) * mm});
            skLineSegment(sketch, "E736", {"start": v(-39.6, 8.62) * mm, "end": v(-40.23, 8.62) * mm});
            skLineSegment(sketch, "E737", {"start": v(-40.23, 8.62) * mm, "end": v(-40.87, 8.62) * mm});
            skLineSegment(sketch, "E738", {"start": v(-40.87, 8.62) * mm, "end": v(-41.5, 8.62) * mm});
            skLineSegment(sketch, "E739", {"start": v(-41.5, 8.62) * mm, "end": v(-42.14, 8.62) * mm});
            skLineSegment(sketch, "E740", {"start": v(-42.14, 8.62) * mm, "end": v(-42.77, 8.62) * mm});
            skLineSegment(sketch, "E741", {"start": v(-42.77, 8.62) * mm, "end": v(-43.4, 8.61) * mm});
            skLineSegment(sketch, "E742", {"start": v(-43.4, 8.61) * mm, "end": v(-44.04, 8.61) * mm});
            skLineSegment(sketch, "E743", {"start": v(-44.04, 8.61) * mm, "end": v(-44.68, 8.6) * mm});
            skLineSegment(sketch, "E744", {"start": v(-44.68, 8.6) * mm, "end": v(-45.31, 8.6) * mm});
            skLineSegment(sketch, "E745", {"start": v(-45.31, 8.6) * mm, "end": v(-45.95, 8.6) * mm});
            skLineSegment(sketch, "E746", {"start": v(-45.95, 8.6) * mm, "end": v(-46.58, 8.6) * mm});
            skLineSegment(sketch, "E747", {"start": v(-46.58, 8.6) * mm, "end": v(-47.22, 8.59) * mm});
            skLineSegment(sketch, "E748", {"start": v(-47.22, 8.59) * mm, "end": v(-47.85, 8.58) * mm});
            skLineSegment(sketch, "E749", {"start": v(-47.85, 8.58) * mm, "end": v(-48.49, 8.58) * mm});
            skLineSegment(sketch, "E750", {"start": v(-48.49, 8.58) * mm, "end": v(-49.12, 8.57) * mm});
            skLineSegment(sketch, "E751", {"start": v(-49.12, 8.57) * mm, "end": v(-49.76, 8.56) * mm});
            skLineSegment(sketch, "E752", {"start": v(-49.76, 8.56) * mm, "end": v(-50.4, 8.55) * mm});
            skLineSegment(sketch, "E753", {"start": v(-50.4, 8.55) * mm, "end": v(-51.03, 8.54) * mm});
            skLineSegment(sketch, "E754", {"start": v(-51.03, 8.54) * mm, "end": v(-51.66, 8.53) * mm});
            skLineSegment(sketch, "E755", {"start": v(-51.66, 8.53) * mm, "end": v(-52.3, 8.52) * mm});
            skLineSegment(sketch, "E756", {"start": v(-52.3, 8.52) * mm, "end": v(-52.93, 8.5) * mm});
            skLineSegment(sketch, "E757", {"start": v(-52.93, 8.5) * mm, "end": v(-53.57, 8.5) * mm});
            skLineSegment(sketch, "E758", {"start": v(-53.57, 8.5) * mm, "end": v(-54.2, 8.48) * mm});
            skLineSegment(sketch, "E759", {"start": v(-54.2, 8.48) * mm, "end": v(-54.84, 8.47) * mm});
            skLineSegment(sketch, "E760", {"start": v(-54.84, 8.47) * mm, "end": v(-55.47, 8.45) * mm});
            skLineSegment(sketch, "E761", {"start": v(-55.47, 8.45) * mm, "end": v(-56.1, 8.44) * mm});
            skLineSegment(sketch, "E762", {"start": v(-56.1, 8.44) * mm, "end": v(-56.74, 8.42) * mm});
            skLineSegment(sketch, "E763", {"start": v(-56.74, 8.42) * mm, "end": v(-57.37, 8.4) * mm});
            skLineSegment(sketch, "E764", {"start": v(-57.37, 8.4) * mm, "end": v(-58, 8.39) * mm});
            skLineSegment(sketch, "E765", {"start": v(-58, 8.39) * mm, "end": v(-58.64, 8.37) * mm});
            skLineSegment(sketch, "E766", {"start": v(-58.64, 8.37) * mm, "end": v(-59.28, 8.35) * mm});
            skLineSegment(sketch, "E767", {"start": v(-59.28, 8.35) * mm, "end": v(-59.91, 8.33) * mm});
            skLineSegment(sketch, "E768", {"start": v(-59.91, 8.33) * mm, "end": v(-60.55, 8.3) * mm});
            skLineSegment(sketch, "E769", {"start": v(-60.55, 8.3) * mm, "end": v(-61.18, 8.29) * mm});
            skLineSegment(sketch, "E770", {"start": v(-61.18, 8.29) * mm, "end": v(-61.82, 8.27) * mm});
            skLineSegment(sketch, "E771", {"start": v(-61.82, 8.27) * mm, "end": v(-62.45, 8.24) * mm});
            skLineSegment(sketch, "E772", {"start": v(-62.45, 8.24) * mm, "end": v(-63.09, 8.22) * mm});
            skLineSegment(sketch, "E773", {"start": v(-63.09, 8.22) * mm, "end": v(-63.72, 8.2) * mm});
            skLineSegment(sketch, "E774", {"start": v(-63.72, 8.2) * mm, "end": v(-64.36, 8.17) * mm});
            skLineSegment(sketch, "E775", {"start": v(-64.36, 8.17) * mm, "end": v(-65, 8.14) * mm});
            skLineSegment(sketch, "E776", {"start": v(-65, 8.14) * mm, "end": v(-65.63, 8.12) * mm});
            skLineSegment(sketch, "E777", {"start": v(-65.63, 8.12) * mm, "end": v(-66.26, 8.09) * mm});
            skLineSegment(sketch, "E778", {"start": v(-66.26, 8.09) * mm, "end": v(-66.9, 8.06) * mm});
            skLineSegment(sketch, "E779", {"start": v(-66.9, 8.06) * mm, "end": v(-67.53, 8.03) * mm});
            skLineSegment(sketch, "E780", {"start": v(-67.53, 8.03) * mm, "end": v(-68.16, 8) * mm});
            skLineSegment(sketch, "E781", {"start": v(-68.16, 8) * mm, "end": v(-68.8, 7.97) * mm});
            skLineSegment(sketch, "E782", {"start": v(-68.8, 7.97) * mm, "end": v(-69.43, 7.94) * mm});
            skLineSegment(sketch, "E783", {"start": v(-69.43, 7.94) * mm, "end": v(-70.07, 7.9) * mm});
            skLineSegment(sketch, "E784", {"start": v(-70.07, 7.9) * mm, "end": v(-70.7, 7.87) * mm});
            skLineSegment(sketch, "E785", {"start": v(-70.7, 7.87) * mm, "end": v(-71.34, 7.84) * mm});
            skLineSegment(sketch, "E786", {"start": v(-71.34, 7.84) * mm, "end": v(-71.97, 7.8) * mm});
            skLineSegment(sketch, "E787", {"start": v(-71.97, 7.8) * mm, "end": v(-72.6, 7.76) * mm});
            skLineSegment(sketch, "E788", {"start": v(-72.6, 7.76) * mm, "end": v(-73.24, 7.73) * mm});
            skLineSegment(sketch, "E789", {"start": v(-73.24, 7.73) * mm, "end": v(-73.88, 7.69) * mm});
            skLineSegment(sketch, "E790", {"start": v(-73.88, 7.69) * mm, "end": v(-74.51, 7.65) * mm});
            skLineSegment(sketch, "E791", {"start": v(-74.51, 7.65) * mm, "end": v(-75.15, 7.6) * mm});
            skLineSegment(sketch, "E792", {"start": v(-75.15, 7.6) * mm, "end": v(-75.78, 7.57) * mm});
            skLineSegment(sketch, "E793", {"start": v(-75.78, 7.57) * mm, "end": v(-76.42, 7.52) * mm});
            skLineSegment(sketch, "E794", {"start": v(-76.42, 7.52) * mm, "end": v(-77.05, 7.48) * mm});
            skLineSegment(sketch, "E795", {"start": v(-77.05, 7.48) * mm, "end": v(-77.68, 7.44) * mm});
            skLineSegment(sketch, "E796", {"start": v(-77.68, 7.44) * mm, "end": v(-78.32, 7.39) * mm});
            skLineSegment(sketch, "E797", {"start": v(-78.32, 7.39) * mm, "end": v(-78.95, 7.34) * mm});
            skLineSegment(sketch, "E798", {"start": v(-78.95, 7.34) * mm, "end": v(-79.59, 7.3) * mm});
            skLineSegment(sketch, "E799", {"start": v(-79.59, 7.3) * mm, "end": v(-80.22, 7.24) * mm});
            skLineSegment(sketch, "E800", {"start": v(-80.22, 7.24) * mm, "end": v(-80.86, 7.2) * mm});
            skLineSegment(sketch, "E801", {"start": v(-80.86, 7.2) * mm, "end": v(-81.5, 7.14) * mm});
            skLineSegment(sketch, "E802", {"start": v(-81.5, 7.14) * mm, "end": v(-82.13, 7.09) * mm});
            skLineSegment(sketch, "E803", {"start": v(-82.13, 7.09) * mm, "end": v(-82.76, 7.03) * mm});
            skLineSegment(sketch, "E804", {"start": v(-82.76, 7.03) * mm, "end": v(-83.4, 6.98) * mm});
            skLineSegment(sketch, "E805", {"start": v(-83.4, 6.98) * mm, "end": v(-84.03, 6.92) * mm});
            skLineSegment(sketch, "E806", {"start": v(-84.03, 6.92) * mm, "end": v(-84.67, 6.86) * mm});
            skLineSegment(sketch, "E807", {"start": v(-84.67, 6.86) * mm, "end": v(-85.3, 6.8) * mm});
            skLineSegment(sketch, "E808", {"start": v(-85.3, 6.8) * mm, "end": v(-85.93, 6.74) * mm});
            skLineSegment(sketch, "E809", {"start": v(-85.93, 6.74) * mm, "end": v(-86.57, 6.68) * mm});
            skLineSegment(sketch, "E810", {"start": v(-86.57, 6.68) * mm, "end": v(-87.2, 6.61) * mm});
            skLineSegment(sketch, "E811", {"start": v(-87.2, 6.61) * mm, "end": v(-87.84, 6.55) * mm});
            skLineSegment(sketch, "E812", {"start": v(-87.84, 6.55) * mm, "end": v(-88.47, 6.48) * mm});
            skLineSegment(sketch, "E813", {"start": v(-88.47, 6.48) * mm, "end": v(-89.1, 6.4) * mm});
            skLineSegment(sketch, "E814", {"start": v(-89.1, 6.4) * mm, "end": v(-89.74, 6.34) * mm});
            skLineSegment(sketch, "E815", {"start": v(-89.74, 6.34) * mm, "end": v(-90.38, 6.27) * mm});
            skLineSegment(sketch, "E816", {"start": v(-90.38, 6.27) * mm, "end": v(-91.01, 6.2) * mm});
            skLineSegment(sketch, "E817", {"start": v(-91.01, 6.2) * mm, "end": v(-91.64, 6.12) * mm});
            skLineSegment(sketch, "E818", {"start": v(-91.64, 6.12) * mm, "end": v(-92.28, 6.04) * mm});
            skLineSegment(sketch, "E819", {"start": v(-92.28, 6.04) * mm, "end": v(-92.91, 5.96) * mm});
            skLineSegment(sketch, "E820", {"start": v(-92.91, 5.96) * mm, "end": v(-93.55, 5.88) * mm});
            skLineSegment(sketch, "E821", {"start": v(-93.55, 5.88) * mm, "end": v(-94.18, 5.8) * mm});
            skLineSegment(sketch, "E822", {"start": v(-94.18, 5.8) * mm, "end": v(-94.82, 5.71) * mm});
            skLineSegment(sketch, "E823", {"start": v(-94.82, 5.71) * mm, "end": v(-95.45, 5.63) * mm});
            skLineSegment(sketch, "E824", {"start": v(-95.45, 5.63) * mm, "end": v(-96.09, 5.54) * mm});
            skLineSegment(sketch, "E825", {"start": v(-96.09, 5.54) * mm, "end": v(-96.72, 5.45) * mm});
            skLineSegment(sketch, "E826", {"start": v(-96.72, 5.45) * mm, "end": v(-97.35, 5.36) * mm});
            skLineSegment(sketch, "E827", {"start": v(-97.35, 5.36) * mm, "end": v(-97.99, 5.26) * mm});
            skLineSegment(sketch, "E828", {"start": v(-97.99, 5.26) * mm, "end": v(-98.62, 5.17) * mm});
            skLineSegment(sketch, "E829", {"start": v(-98.62, 5.17) * mm, "end": v(-99.26, 5.07) * mm});
            skLineSegment(sketch, "E830", {"start": v(-99.26, 5.07) * mm, "end": v(-99.9, 4.97) * mm});
            skLineSegment(sketch, "E831", {"start": v(-99.9, 4.97) * mm, "end": v(-100.52, 4.86) * mm});
            skLineSegment(sketch, "E832", {"start": v(-100.52, 4.86) * mm, "end": v(-101.16, 4.76) * mm});
            skLineSegment(sketch, "E833", {"start": v(-101.16, 4.76) * mm, "end": v(-101.8, 4.65) * mm});
            skLineSegment(sketch, "E834", {"start": v(-101.8, 4.65) * mm, "end": v(-102.43, 4.54) * mm});
            skLineSegment(sketch, "E835", {"start": v(-102.43, 4.54) * mm, "end": v(-103.06, 4.42) * mm});
            skLineSegment(sketch, "E836", {"start": v(-103.06, 4.42) * mm, "end": v(-103.7, 4.3) * mm});
            skLineSegment(sketch, "E837", {"start": v(-103.7, 4.3) * mm, "end": v(-104.33, 4.19) * mm});
            skLineSegment(sketch, "E838", {"start": v(-104.33, 4.19) * mm, "end": v(-104.96, 4.06) * mm});
            skLineSegment(sketch, "E839", {"start": v(-104.96, 4.06) * mm, "end": v(-105.6, 3.94) * mm});
            skLineSegment(sketch, "E840", {"start": v(-105.6, 3.94) * mm, "end": v(-106.23, 3.8) * mm});
            skLineSegment(sketch, "E841", {"start": v(-106.23, 3.8) * mm, "end": v(-106.87, 3.68) * mm});
            skLineSegment(sketch, "E842", {"start": v(-106.87, 3.68) * mm, "end": v(-107.5, 3.54) * mm});
            skLineSegment(sketch, "E843", {"start": v(-107.5, 3.54) * mm, "end": v(-108.13, 3.4) * mm});
            skLineSegment(sketch, "E844", {"start": v(-108.13, 3.4) * mm, "end": v(-108.77, 3.26) * mm});
            skLineSegment(sketch, "E845", {"start": v(-108.77, 3.26) * mm, "end": v(-109.4, 3.11) * mm});
            skLineSegment(sketch, "E846", {"start": v(-109.4, 3.11) * mm, "end": v(-110.03, 2.96) * mm});
            skLineSegment(sketch, "E847", {"start": v(-110.03, 2.96) * mm, "end": v(-110.67, 2.8) * mm});
            skLineSegment(sketch, "E848", {"start": v(-110.67, 2.8) * mm, "end": v(-111.3, 2.65) * mm});
            skLineSegment(sketch, "E849", {"start": v(-111.3, 2.65) * mm, "end": v(-111.93, 2.48) * mm});
            skLineSegment(sketch, "E850", {"start": v(-111.93, 2.48) * mm, "end": v(-112.57, 2.31) * mm});
            skLineSegment(sketch, "E851", {"start": v(-112.57, 2.31) * mm, "end": v(-113.2, 2.14) * mm});
            skLineSegment(sketch, "E852", {"start": v(-113.2, 2.14) * mm, "end": v(-113.83, 1.96) * mm});
            skLineSegment(sketch, "E853", {"start": v(-113.83, 1.96) * mm, "end": v(-114.47, 1.77) * mm});
            skLineSegment(sketch, "E854", {"start": v(-114.47, 1.77) * mm, "end": v(-115.1, 1.58) * mm});
            skLineSegment(sketch, "E855", {"start": v(-115.1, 1.58) * mm, "end": v(-115.73, 1.38) * mm});
            skLineSegment(sketch, "E856", {"start": v(-115.73, 1.38) * mm, "end": v(-116.37, 1.17) * mm});
            skLineSegment(sketch, "E857", {"start": v(-116.37, 1.17) * mm, "end": v(-117, 0.96) * mm});
            skLineSegment(sketch, "E858", {"start": v(61.37, -4.36) * mm, "end": v(60.74, -4.38) * mm});
            skLineSegment(sketch, "E859", {"start": v(60.74, -4.38) * mm, "end": v(60.1, -4.4) * mm});
            skLineSegment(sketch, "E860", {"start": v(60.1, -4.4) * mm, "end": v(59.47, -4.43) * mm});
            skLineSegment(sketch, "E861", {"start": v(59.47, -4.43) * mm, "end": v(58.83, -4.46) * mm});
            skLineSegment(sketch, "E862", {"start": v(58.83, -4.46) * mm, "end": v(58.2, -4.48) * mm});
            skLineSegment(sketch, "E863", {"start": v(58.2, -4.48) * mm, "end": v(57.56, -4.51) * mm});
            skLineSegment(sketch, "E864", {"start": v(57.56, -4.51) * mm, "end": v(56.93, -4.54) * mm});
            skLineSegment(sketch, "E865", {"start": v(56.93, -4.54) * mm, "end": v(56.3, -4.56) * mm});
            skLineSegment(sketch, "E866", {"start": v(56.3, -4.56) * mm, "end": v(55.66, -4.59) * mm});
            skLineSegment(sketch, "E867", {"start": v(55.66, -4.59) * mm, "end": v(55.02, -4.61) * mm});
            skLineSegment(sketch, "E868", {"start": v(55.02, -4.61) * mm, "end": v(54.39, -4.64) * mm});
            skLineSegment(sketch, "E869", {"start": v(54.39, -4.64) * mm, "end": v(53.75, -4.66) * mm});
            skLineSegment(sketch, "E870", {"start": v(53.75, -4.66) * mm, "end": v(53.12, -4.7) * mm});
            skLineSegment(sketch, "E871", {"start": v(53.12, -4.7) * mm, "end": v(52.48, -4.72) * mm});
            skLineSegment(sketch, "E872", {"start": v(52.48, -4.72) * mm, "end": v(51.85, -4.74) * mm});
            skLineSegment(sketch, "E873", {"start": v(51.85, -4.74) * mm, "end": v(51.21, -4.77) * mm});
            skLineSegment(sketch, "E874", {"start": v(51.21, -4.77) * mm, "end": v(50.58, -4.8) * mm});
            skLineSegment(sketch, "E875", {"start": v(50.58, -4.8) * mm, "end": v(49.94, -4.82) * mm});
            skLineSegment(sketch, "E876", {"start": v(49.94, -4.82) * mm, "end": v(49.3, -4.85) * mm});
            skLineSegment(sketch, "E877", {"start": v(49.3, -4.85) * mm, "end": v(48.67, -4.87) * mm});
            skLineSegment(sketch, "E878", {"start": v(48.67, -4.87) * mm, "end": v(48.04, -4.9) * mm});
            skLineSegment(sketch, "E879", {"start": v(48.04, -4.9) * mm, "end": v(47.4, -4.92) * mm});
            skLineSegment(sketch, "E880", {"start": v(47.4, -4.92) * mm, "end": v(46.77, -4.95) * mm});
            skLineSegment(sketch, "E881", {"start": v(46.77, -4.95) * mm, "end": v(46.13, -4.98) * mm});
            skLineSegment(sketch, "E882", {"start": v(46.13, -4.98) * mm, "end": v(45.5, -5) * mm});
            skLineSegment(sketch, "E883", {"start": v(45.5, -5) * mm, "end": v(44.86, -5.03) * mm});
            skLineSegment(sketch, "E884", {"start": v(44.86, -5.03) * mm, "end": v(44.23, -5.05) * mm});
            skLineSegment(sketch, "E885", {"start": v(44.23, -5.05) * mm, "end": v(43.6, -5.08) * mm});
            skLineSegment(sketch, "E886", {"start": v(43.6, -5.08) * mm, "end": v(42.96, -5.1) * mm});
            skLineSegment(sketch, "E887", {"start": v(42.96, -5.1) * mm, "end": v(42.32, -5.13) * mm});
            skLineSegment(sketch, "E888", {"start": v(42.32, -5.13) * mm, "end": v(41.69, -5.16) * mm});
            skLineSegment(sketch, "E889", {"start": v(41.69, -5.16) * mm, "end": v(41.05, -5.18) * mm});
            skLineSegment(sketch, "E890", {"start": v(41.05, -5.18) * mm, "end": v(40.42, -5.2) * mm});
            skLineSegment(sketch, "E891", {"start": v(40.42, -5.2) * mm, "end": v(39.78, -5.24) * mm});
            skLineSegment(sketch, "E892", {"start": v(39.78, -5.24) * mm, "end": v(39.15, -5.26) * mm});
            skLineSegment(sketch, "E893", {"start": v(39.15, -5.26) * mm, "end": v(38.51, -5.29) * mm});
            skLineSegment(sketch, "E894", {"start": v(38.51, -5.29) * mm, "end": v(37.88, -5.31) * mm});
            skLineSegment(sketch, "E895", {"start": v(37.88, -5.31) * mm, "end": v(37.24, -5.34) * mm});
            skLineSegment(sketch, "E896", {"start": v(37.24, -5.34) * mm, "end": v(36.6, -5.37) * mm});
            skLineSegment(sketch, "E897", {"start": v(36.6, -5.37) * mm, "end": v(35.97, -5.4) * mm});
            skLineSegment(sketch, "E898", {"start": v(35.97, -5.4) * mm, "end": v(35.34, -5.42) * mm});
            skLineSegment(sketch, "E899", {"start": v(35.34, -5.42) * mm, "end": v(34.7, -5.44) * mm});
            skLineSegment(sketch, "E900", {"start": v(34.7, -5.44) * mm, "end": v(34.07, -5.47) * mm});
            skLineSegment(sketch, "E901", {"start": v(34.07, -5.47) * mm, "end": v(33.43, -5.5) * mm});
            skLineSegment(sketch, "E902", {"start": v(33.43, -5.5) * mm, "end": v(32.8, -5.52) * mm});
            skLineSegment(sketch, "E903", {"start": v(32.8, -5.52) * mm, "end": v(32.16, -5.55) * mm});
            skLineSegment(sketch, "E904", {"start": v(32.16, -5.55) * mm, "end": v(31.53, -5.57) * mm});
            skLineSegment(sketch, "E905", {"start": v(31.53, -5.57) * mm, "end": v(30.9, -5.6) * mm});
            skLineSegment(sketch, "E906", {"start": v(30.9, -5.6) * mm, "end": v(30.26, -5.63) * mm});
            skLineSegment(sketch, "E907", {"start": v(30.26, -5.63) * mm, "end": v(29.62, -5.65) * mm});
            skLineSegment(sketch, "E908", {"start": v(29.62, -5.65) * mm, "end": v(28.99, -5.68) * mm});
            skLineSegment(sketch, "E909", {"start": v(28.99, -5.68) * mm, "end": v(28.35, -5.7) * mm});
            skLineSegment(sketch, "E910", {"start": v(28.35, -5.7) * mm, "end": v(27.72, -5.73) * mm});
            skLineSegment(sketch, "E911", {"start": v(27.72, -5.73) * mm, "end": v(27.08, -5.76) * mm});
            skLineSegment(sketch, "E912", {"start": v(27.08, -5.76) * mm, "end": v(26.45, -5.78) * mm});
            skLineSegment(sketch, "E913", {"start": v(26.45, -5.78) * mm, "end": v(25.81, -5.8) * mm});
            skLineSegment(sketch, "E914", {"start": v(25.81, -5.8) * mm, "end": v(25.18, -5.84) * mm});
            skLineSegment(sketch, "E915", {"start": v(25.18, -5.84) * mm, "end": v(24.54, -5.86) * mm});
            skLineSegment(sketch, "E916", {"start": v(24.54, -5.86) * mm, "end": v(23.9, -5.89) * mm});
            skLineSegment(sketch, "E917", {"start": v(23.9, -5.89) * mm, "end": v(23.27, -5.91) * mm});
            skLineSegment(sketch, "E918", {"start": v(23.27, -5.91) * mm, "end": v(22.64, -5.94) * mm});
            skLineSegment(sketch, "E919", {"start": v(22.64, -5.94) * mm, "end": v(22, -5.97) * mm});
            skLineSegment(sketch, "E920", {"start": v(22, -5.97) * mm, "end": v(21.37, -6) * mm});
            skLineSegment(sketch, "E921", {"start": v(21.37, -6) * mm, "end": v(20.73, -6.02) * mm});
            skLineSegment(sketch, "E922", {"start": v(20.73, -6.02) * mm, "end": v(20.1, -6.04) * mm});
            skLineSegment(sketch, "E923", {"start": v(20.1, -6.04) * mm, "end": v(19.46, -6.07) * mm});
            skLineSegment(sketch, "E924", {"start": v(19.46, -6.07) * mm, "end": v(18.83, -6.1) * mm});
            skLineSegment(sketch, "E925", {"start": v(18.83, -6.1) * mm, "end": v(18.2, -6.12) * mm});
            skLineSegment(sketch, "E926", {"start": v(18.2, -6.12) * mm, "end": v(17.56, -6.15) * mm});
            skLineSegment(sketch, "E927", {"start": v(17.56, -6.15) * mm, "end": v(16.92, -6.17) * mm});
            skLineSegment(sketch, "E928", {"start": v(16.92, -6.17) * mm, "end": v(16.29, -6.2) * mm});
            skLineSegment(sketch, "E929", {"start": v(16.29, -6.2) * mm, "end": v(15.65, -6.22) * mm});
            skLineSegment(sketch, "E930", {"start": v(15.65, -6.22) * mm, "end": v(15.02, -6.25) * mm});
            skLineSegment(sketch, "E931", {"start": v(15.02, -6.25) * mm, "end": v(14.38, -6.27) * mm});
            skLineSegment(sketch, "E932", {"start": v(14.38, -6.27) * mm, "end": v(13.75, -6.3) * mm});
            skLineSegment(sketch, "E933", {"start": v(13.75, -6.3) * mm, "end": v(13.11, -6.32) * mm});
            skLineSegment(sketch, "E934", {"start": v(13.11, -6.32) * mm, "end": v(12.48, -6.35) * mm});
            skLineSegment(sketch, "E935", {"start": v(12.48, -6.35) * mm, "end": v(11.84, -6.37) * mm});
            skLineSegment(sketch, "E936", {"start": v(11.84, -6.37) * mm, "end": v(11.2, -6.4) * mm});
            skLineSegment(sketch, "E937", {"start": v(11.2, -6.4) * mm, "end": v(10.57, -6.42) * mm});
            skLineSegment(sketch, "E938", {"start": v(10.57, -6.42) * mm, "end": v(9.94, -6.45) * mm});
            skLineSegment(sketch, "E939", {"start": v(9.94, -6.45) * mm, "end": v(9.3, -6.47) * mm});
            skLineSegment(sketch, "E940", {"start": v(9.3, -6.47) * mm, "end": v(8.67, -6.5) * mm});
            skLineSegment(sketch, "E941", {"start": v(8.67, -6.5) * mm, "end": v(8.03, -6.52) * mm});
            skLineSegment(sketch, "E942", {"start": v(8.03, -6.52) * mm, "end": v(7.4, -6.55) * mm});
            skLineSegment(sketch, "E943", {"start": v(7.4, -6.55) * mm, "end": v(6.76, -6.57) * mm});
            skLineSegment(sketch, "E944", {"start": v(6.76, -6.57) * mm, "end": v(6.13, -6.6) * mm});
            skLineSegment(sketch, "E945", {"start": v(6.13, -6.6) * mm, "end": v(5.5, -6.62) * mm});
            skLineSegment(sketch, "E946", {"start": v(5.5, -6.62) * mm, "end": v(4.86, -6.64) * mm});
            skLineSegment(sketch, "E947", {"start": v(4.86, -6.64) * mm, "end": v(4.22, -6.67) * mm});
            skLineSegment(sketch, "E948", {"start": v(4.22, -6.67) * mm, "end": v(3.59, -6.7) * mm});
            skLineSegment(sketch, "E949", {"start": v(3.59, -6.7) * mm, "end": v(2.95, -6.72) * mm});
            skLineSegment(sketch, "E950", {"start": v(2.95, -6.72) * mm, "end": v(2.32, -6.74) * mm});
            skLineSegment(sketch, "E951", {"start": v(2.32, -6.74) * mm, "end": v(1.68, -6.76) * mm});
            skLineSegment(sketch, "E952", {"start": v(1.68, -6.76) * mm, "end": v(1.05, -6.79) * mm});
            skLineSegment(sketch, "E953", {"start": v(1.05, -6.79) * mm, "end": v(0.41, -6.81) * mm});
            skLineSegment(sketch, "E954", {"start": v(0.41, -6.81) * mm, "end": v(-0.22, -6.84) * mm});
            skLineSegment(sketch, "E955", {"start": v(-0.22, -6.84) * mm, "end": v(-0.86, -6.86) * mm});
            skLineSegment(sketch, "E956", {"start": v(-0.86, -6.86) * mm, "end": v(-1.5, -6.88) * mm});
            skLineSegment(sketch, "E957", {"start": v(-1.5, -6.88) * mm, "end": v(-2.13, -6.9) * mm});
            skLineSegment(sketch, "E958", {"start": v(-2.13, -6.9) * mm, "end": v(-2.76, -6.93) * mm});
            skLineSegment(sketch, "E959", {"start": v(-2.76, -6.93) * mm, "end": v(-3.4, -6.95) * mm});
            skLineSegment(sketch, "E960", {"start": v(-3.4, -6.95) * mm, "end": v(-4.03, -6.98) * mm});
            skLineSegment(sketch, "E961", {"start": v(-4.03, -6.98) * mm, "end": v(-4.67, -7) * mm});
            skLineSegment(sketch, "E962", {"start": v(-4.67, -7) * mm, "end": v(-5.3, -7.03) * mm});
            skLineSegment(sketch, "E963", {"start": v(-5.3, -7.03) * mm, "end": v(-5.94, -7.05) * mm});
            skLineSegment(sketch, "E964", {"start": v(-5.94, -7.05) * mm, "end": v(-6.57, -7.07) * mm});
            skLineSegment(sketch, "E965", {"start": v(-6.57, -7.07) * mm, "end": v(-7.2, -7.1) * mm});
            skLineSegment(sketch, "E966", {"start": v(-7.2, -7.1) * mm, "end": v(-7.84, -7.12) * mm});
            skLineSegment(sketch, "E967", {"start": v(-7.84, -7.12) * mm, "end": v(-8.48, -7.14) * mm});
            skLineSegment(sketch, "E968", {"start": v(-8.48, -7.14) * mm, "end": v(-9.11, -7.16) * mm});
            skLineSegment(sketch, "E969", {"start": v(-9.11, -7.16) * mm, "end": v(-9.75, -7.19) * mm});
            skLineSegment(sketch, "E970", {"start": v(-9.75, -7.19) * mm, "end": v(-10.38, -7.2) * mm});
            skLineSegment(sketch, "E971", {"start": v(-10.38, -7.2) * mm, "end": v(-11.02, -7.23) * mm});
            skLineSegment(sketch, "E972", {"start": v(-11.02, -7.23) * mm, "end": v(-11.65, -7.25) * mm});
            skLineSegment(sketch, "E973", {"start": v(-11.65, -7.25) * mm, "end": v(-12.29, -7.28) * mm});
            skLineSegment(sketch, "E974", {"start": v(-12.29, -7.28) * mm, "end": v(-12.92, -7.3) * mm});
            skLineSegment(sketch, "E975", {"start": v(-12.92, -7.3) * mm, "end": v(-13.56, -7.32) * mm});
            skLineSegment(sketch, "E976", {"start": v(-13.56, -7.32) * mm, "end": v(-14.2, -7.34) * mm});
            skLineSegment(sketch, "E977", {"start": v(-14.2, -7.34) * mm, "end": v(-14.83, -7.36) * mm});
            skLineSegment(sketch, "E978", {"start": v(-14.83, -7.36) * mm, "end": v(-15.46, -7.38) * mm});
            skLineSegment(sketch, "E979", {"start": v(-15.46, -7.38) * mm, "end": v(-16.1, -7.4) * mm});
            skLineSegment(sketch, "E980", {"start": v(-16.1, -7.4) * mm, "end": v(-16.73, -7.43) * mm});
            skLineSegment(sketch, "E981", {"start": v(-16.73, -7.43) * mm, "end": v(-17.37, -7.45) * mm});
            skLineSegment(sketch, "E982", {"start": v(-17.37, -7.45) * mm, "end": v(-18, -7.47) * mm});
            skLineSegment(sketch, "E983", {"start": v(-18, -7.47) * mm, "end": v(-18.64, -7.5) * mm});
            skLineSegment(sketch, "E984", {"start": v(-18.64, -7.5) * mm, "end": v(-19.27, -7.51) * mm});
            skLineSegment(sketch, "E985", {"start": v(-19.27, -7.51) * mm, "end": v(-19.9, -7.53) * mm});
            skLineSegment(sketch, "E986", {"start": v(-19.9, -7.53) * mm, "end": v(-20.54, -7.55) * mm});
            skLineSegment(sketch, "E987", {"start": v(-20.54, -7.55) * mm, "end": v(-21.18, -7.58) * mm});
            skLineSegment(sketch, "E988", {"start": v(-21.18, -7.58) * mm, "end": v(-21.81, -7.6) * mm});
            skLineSegment(sketch, "E989", {"start": v(-21.81, -7.6) * mm, "end": v(-22.45, -7.62) * mm});
            skLineSegment(sketch, "E990", {"start": v(-22.45, -7.62) * mm, "end": v(-23.08, -7.64) * mm});
            skLineSegment(sketch, "E991", {"start": v(-23.08, -7.64) * mm, "end": v(-23.72, -7.66) * mm});
            skLineSegment(sketch, "E992", {"start": v(-23.72, -7.66) * mm, "end": v(-24.35, -7.68) * mm});
            skLineSegment(sketch, "E993", {"start": v(-24.35, -7.68) * mm, "end": v(-24.99, -7.7) * mm});
            skLineSegment(sketch, "E994", {"start": v(-24.99, -7.7) * mm, "end": v(-25.62, -7.72) * mm});
            skLineSegment(sketch, "E995", {"start": v(-25.62, -7.72) * mm, "end": v(-26.26, -7.74) * mm});
            skLineSegment(sketch, "E996", {"start": v(-26.26, -7.74) * mm, "end": v(-26.9, -7.76) * mm});
            skLineSegment(sketch, "E997", {"start": v(-26.9, -7.76) * mm, "end": v(-27.53, -7.77) * mm});
            skLineSegment(sketch, "E998", {"start": v(-27.53, -7.77) * mm, "end": v(-28.16, -7.8) * mm});
            skLineSegment(sketch, "E999", {"start": v(-28.16, -7.8) * mm, "end": v(-28.8, -7.81) * mm});
            skLineSegment(sketch, "E1000", {"start": v(-28.8, -7.81) * mm, "end": v(-29.43, -7.83) * mm});
            skLineSegment(sketch, "E1001", {"start": v(-29.43, -7.83) * mm, "end": v(-30.07, -7.85) * mm});
            skLineSegment(sketch, "E1002", {"start": v(-30.07, -7.85) * mm, "end": v(-30.7, -7.87) * mm});
            skLineSegment(sketch, "E1003", {"start": v(-30.7, -7.87) * mm, "end": v(-31.34, -7.89) * mm});
            skLineSegment(sketch, "E1004", {"start": v(-31.34, -7.89) * mm, "end": v(-31.97, -7.9) * mm});
            skLineSegment(sketch, "E1005", {"start": v(-31.97, -7.9) * mm, "end": v(-32.6, -7.92) * mm});
            skLineSegment(sketch, "E1006", {"start": v(-32.6, -7.92) * mm, "end": v(-33.24, -7.94) * mm});
            skLineSegment(sketch, "E1007", {"start": v(-33.24, -7.94) * mm, "end": v(-33.88, -7.96) * mm});
            skLineSegment(sketch, "E1008", {"start": v(-33.88, -7.96) * mm, "end": v(-34.51, -7.98) * mm});
            skLineSegment(sketch, "E1009", {"start": v(-34.51, -7.98) * mm, "end": v(-35.15, -8) * mm});
            skLineSegment(sketch, "E1010", {"start": v(-35.15, -8) * mm, "end": v(-35.78, -8.01) * mm});
            skLineSegment(sketch, "E1011", {"start": v(-35.78, -8.01) * mm, "end": v(-36.42, -8.03) * mm});
            skLineSegment(sketch, "E1012", {"start": v(-36.42, -8.03) * mm, "end": v(-37.05, -8.05) * mm});
            skLineSegment(sketch, "E1013", {"start": v(-37.05, -8.05) * mm, "end": v(-37.69, -8.06) * mm});
            skLineSegment(sketch, "E1014", {"start": v(-37.69, -8.06) * mm, "end": v(-38.32, -8.08) * mm});
            skLineSegment(sketch, "E1015", {"start": v(-38.32, -8.08) * mm, "end": v(-38.96, -8.1) * mm});
            skLineSegment(sketch, "E1016", {"start": v(-38.96, -8.1) * mm, "end": v(-39.6, -8.11) * mm});
            skLineSegment(sketch, "E1017", {"start": v(-39.6, -8.11) * mm, "end": v(-40.23, -8.13) * mm});
            skLineSegment(sketch, "E1018", {"start": v(-40.23, -8.13) * mm, "end": v(-40.86, -8.14) * mm});
            skLineSegment(sketch, "E1019", {"start": v(-40.86, -8.14) * mm, "end": v(-41.5, -8.16) * mm});
            skLineSegment(sketch, "E1020", {"start": v(-41.5, -8.16) * mm, "end": v(-42.13, -8.17) * mm});
            skLineSegment(sketch, "E1021", {"start": v(-42.13, -8.17) * mm, "end": v(-42.77, -8.19) * mm});
            skLineSegment(sketch, "E1022", {"start": v(-42.77, -8.19) * mm, "end": v(-43.4, -8.2) * mm});
            skLineSegment(sketch, "E1023", {"start": v(-43.4, -8.2) * mm, "end": v(-44.04, -8.22) * mm});
            skLineSegment(sketch, "E1024", {"start": v(-44.04, -8.22) * mm, "end": v(-44.68, -8.23) * mm});
            skLineSegment(sketch, "E1025", {"start": v(-44.68, -8.23) * mm, "end": v(-45.31, -8.25) * mm});
            skLineSegment(sketch, "E1026", {"start": v(-45.31, -8.25) * mm, "end": v(-45.95, -8.26) * mm});
            skLineSegment(sketch, "E1027", {"start": v(-45.95, -8.26) * mm, "end": v(-46.58, -8.28) * mm});
            skLineSegment(sketch, "E1028", {"start": v(-46.58, -8.28) * mm, "end": v(-47.22, -8.3) * mm});
            skLineSegment(sketch, "E1029", {"start": v(-47.22, -8.3) * mm, "end": v(-47.85, -8.3) * mm});
            skLineSegment(sketch, "E1030", {"start": v(-47.85, -8.3) * mm, "end": v(-48.49, -8.32) * mm});
            skLineSegment(sketch, "E1031", {"start": v(-48.49, -8.32) * mm, "end": v(-49.12, -8.33) * mm});
            skLineSegment(sketch, "E1032", {"start": v(-49.12, -8.33) * mm, "end": v(-49.76, -8.34) * mm});
            skLineSegment(sketch, "E1033", {"start": v(-49.76, -8.34) * mm, "end": v(-50.4, -8.36) * mm});
            skLineSegment(sketch, "E1034", {"start": v(-50.4, -8.36) * mm, "end": v(-51.03, -8.37) * mm});
            skLineSegment(sketch, "E1035", {"start": v(-51.03, -8.37) * mm, "end": v(-51.66, -8.38) * mm});
            skLineSegment(sketch, "E1036", {"start": v(-51.66, -8.38) * mm, "end": v(-52.3, -8.4) * mm});
            skLineSegment(sketch, "E1037", {"start": v(-52.3, -8.4) * mm, "end": v(-52.93, -8.4) * mm});
            skLineSegment(sketch, "E1038", {"start": v(-52.93, -8.4) * mm, "end": v(-53.57, -8.42) * mm});
            skLineSegment(sketch, "E1039", {"start": v(-53.57, -8.42) * mm, "end": v(-54.2, -8.43) * mm});
            skLineSegment(sketch, "E1040", {"start": v(-54.2, -8.43) * mm, "end": v(-54.84, -8.44) * mm});
            skLineSegment(sketch, "E1041", {"start": v(-54.84, -8.44) * mm, "end": v(-55.47, -8.45) * mm});
            skLineSegment(sketch, "E1042", {"start": v(-55.47, -8.45) * mm, "end": v(-56.1, -8.46) * mm});
            skLineSegment(sketch, "E1043", {"start": v(-56.1, -8.46) * mm, "end": v(-56.74, -8.47) * mm});
            skLineSegment(sketch, "E1044", {"start": v(-56.74, -8.47) * mm, "end": v(-57.38, -8.48) * mm});
            skLineSegment(sketch, "E1045", {"start": v(-57.38, -8.48) * mm, "end": v(-58.01, -8.5) * mm});
            skLineSegment(sketch, "E1046", {"start": v(-58.01, -8.5) * mm, "end": v(-58.65, -8.5) * mm});
            skLineSegment(sketch, "E1047", {"start": v(-58.65, -8.5) * mm, "end": v(-59.28, -8.5) * mm});
            skLineSegment(sketch, "E1048", {"start": v(-59.28, -8.5) * mm, "end": v(-59.92, -8.52) * mm});
            skLineSegment(sketch, "E1049", {"start": v(-59.92, -8.52) * mm, "end": v(-60.55, -8.53) * mm});
            skLineSegment(sketch, "E1050", {"start": v(-60.55, -8.53) * mm, "end": v(-61.19, -8.53) * mm});
            skLineSegment(sketch, "E1051", {"start": v(-61.19, -8.53) * mm, "end": v(-61.82, -8.54) * mm});
            skLineSegment(sketch, "E1052", {"start": v(-61.82, -8.54) * mm, "end": v(-62.46, -8.55) * mm});
            skLineSegment(sketch, "E1053", {"start": v(-62.46, -8.55) * mm, "end": v(-63.1, -8.56) * mm});
            skLineSegment(sketch, "E1054", {"start": v(-63.1, -8.56) * mm, "end": v(-63.73, -8.56) * mm});
            skLineSegment(sketch, "E1055", {"start": v(-63.73, -8.56) * mm, "end": v(-64.36, -8.57) * mm});
            skLineSegment(sketch, "E1056", {"start": v(-64.36, -8.57) * mm, "end": v(-65, -8.57) * mm});
            skLineSegment(sketch, "E1057", {"start": v(-65, -8.57) * mm, "end": v(-65.63, -8.58) * mm});
            skLineSegment(sketch, "E1058", {"start": v(-65.63, -8.58) * mm, "end": v(-66.27, -8.59) * mm});
            skLineSegment(sketch, "E1059", {"start": v(-66.27, -8.59) * mm, "end": v(-66.9, -8.6) * mm});
            skLineSegment(sketch, "E1060", {"start": v(-66.9, -8.6) * mm, "end": v(-67.54, -8.6) * mm});
            skLineSegment(sketch, "E1061", {"start": v(-67.54, -8.6) * mm, "end": v(-68.17, -8.6) * mm});
            skLineSegment(sketch, "E1062", {"start": v(-68.17, -8.6) * mm, "end": v(-68.8, -8.6) * mm});
            skLineSegment(sketch, "E1063", {"start": v(-68.8, -8.6) * mm, "end": v(-69.44, -8.6) * mm});
            skLineSegment(sketch, "E1064", {"start": v(-69.44, -8.6) * mm, "end": v(-70.08, -8.6) * mm});
            skLineSegment(sketch, "E1065", {"start": v(-70.08, -8.6) * mm, "end": v(-70.71, -8.61) * mm});
            skLineSegment(sketch, "E1066", {"start": v(-70.71, -8.61) * mm, "end": v(-71.35, -8.61) * mm});
            skLineSegment(sketch, "E1067", {"start": v(-71.35, -8.61) * mm, "end": v(-71.98, -8.62) * mm});
            skLineSegment(sketch, "E1068", {"start": v(-71.98, -8.62) * mm, "end": v(-72.62, -8.62) * mm});
            skLineSegment(sketch, "E1069", {"start": v(-72.62, -8.62) * mm, "end": v(-73.25, -8.62) * mm});
            skLineSegment(sketch, "E1070", {"start": v(-73.25, -8.62) * mm, "end": v(-73.89, -8.62) * mm});
            skLineSegment(sketch, "E1071", {"start": v(-73.89, -8.62) * mm, "end": v(-74.52, -8.62) * mm});
            skLineSegment(sketch, "E1072", {"start": v(-74.52, -8.62) * mm, "end": v(-75.16, -8.62) * mm});
            skLineSegment(sketch, "E1073", {"start": v(-75.16, -8.62) * mm, "end": v(-75.8, -8.62) * mm});
            skLineSegment(sketch, "E1074", {"start": v(-75.8, -8.62) * mm, "end": v(-76.43, -8.62) * mm});
            skLineSegment(sketch, "E1075", {"start": v(-76.43, -8.62) * mm, "end": v(-77.06, -8.61) * mm});
            skLineSegment(sketch, "E1076", {"start": v(-77.06, -8.61) * mm, "end": v(-77.7, -8.61) * mm});
            skLineSegment(sketch, "E1077", {"start": v(-77.7, -8.61) * mm, "end": v(-78.33, -8.6) * mm});
            skLineSegment(sketch, "E1078", {"start": v(-78.33, -8.6) * mm, "end": v(-78.97, -8.6) * mm});
            skLineSegment(sketch, "E1079", {"start": v(-78.97, -8.6) * mm, "end": v(-79.6, -8.6) * mm});
            skLineSegment(sketch, "E1080", {"start": v(-79.6, -8.6) * mm, "end": v(-80.24, -8.6) * mm});
            skLineSegment(sketch, "E1081", {"start": v(-80.24, -8.6) * mm, "end": v(-80.87, -8.59) * mm});
            skLineSegment(sketch, "E1082", {"start": v(-80.87, -8.59) * mm, "end": v(-81.5, -8.58) * mm});
            skLineSegment(sketch, "E1083", {"start": v(-81.5, -8.58) * mm, "end": v(-82.14, -8.58) * mm});
            skLineSegment(sketch, "E1084", {"start": v(-82.14, -8.58) * mm, "end": v(-82.78, -8.57) * mm});
            skLineSegment(sketch, "E1085", {"start": v(-82.78, -8.57) * mm, "end": v(-83.41, -8.56) * mm});
            skLineSegment(sketch, "E1086", {"start": v(-83.41, -8.56) * mm, "end": v(-84.05, -8.55) * mm});
            skLineSegment(sketch, "E1087", {"start": v(-84.05, -8.55) * mm, "end": v(-84.68, -8.54) * mm});
            skLineSegment(sketch, "E1088", {"start": v(-84.68, -8.54) * mm, "end": v(-85.32, -8.53) * mm});
            skLineSegment(sketch, "E1089", {"start": v(-85.32, -8.53) * mm, "end": v(-85.95, -8.52) * mm});
            skLineSegment(sketch, "E1090", {"start": v(-85.95, -8.52) * mm, "end": v(-86.59, -8.51) * mm});
            skLineSegment(sketch, "E1091", {"start": v(-86.59, -8.51) * mm, "end": v(-87.22, -8.5) * mm});
            skLineSegment(sketch, "E1092", {"start": v(-87.22, -8.5) * mm, "end": v(-87.86, -8.49) * mm});
            skLineSegment(sketch, "E1093", {"start": v(-87.86, -8.49) * mm, "end": v(-88.5, -8.47) * mm});
            skLineSegment(sketch, "E1094", {"start": v(-88.5, -8.47) * mm, "end": v(-89.13, -8.46) * mm});
            skLineSegment(sketch, "E1095", {"start": v(-89.13, -8.46) * mm, "end": v(-89.76, -8.44) * mm});
            skLineSegment(sketch, "E1096", {"start": v(-89.76, -8.44) * mm, "end": v(-90.4, -8.43) * mm});
            skLineSegment(sketch, "E1097", {"start": v(-90.4, -8.43) * mm, "end": v(-91.03, -8.4) * mm});
            skLineSegment(sketch, "E1098", {"start": v(-91.03, -8.4) * mm, "end": v(-91.66, -8.4) * mm});
            skLineSegment(sketch, "E1099", {"start": v(-91.66, -8.4) * mm, "end": v(-92.3, -8.37) * mm});
            skLineSegment(sketch, "E1100", {"start": v(-92.3, -8.37) * mm, "end": v(-92.93, -8.35) * mm});
            skLineSegment(sketch, "E1101", {"start": v(-92.93, -8.35) * mm, "end": v(-93.57, -8.33) * mm});
            skLineSegment(sketch, "E1102", {"start": v(-93.57, -8.33) * mm, "end": v(-94.2, -8.31) * mm});
            skLineSegment(sketch, "E1103", {"start": v(-94.2, -8.31) * mm, "end": v(-94.84, -8.29) * mm});
            skLineSegment(sketch, "E1104", {"start": v(-94.84, -8.29) * mm, "end": v(-95.47, -8.26) * mm});
            skLineSegment(sketch, "E1105", {"start": v(-95.47, -8.26) * mm, "end": v(-96.1, -8.24) * mm});
            skLineSegment(sketch, "E1106", {"start": v(-96.1, -8.24) * mm, "end": v(-96.74, -8.21) * mm});
            skLineSegment(sketch, "E1107", {"start": v(-96.74, -8.21) * mm, "end": v(-97.38, -8.19) * mm});
            skLineSegment(sketch, "E1108", {"start": v(-97.38, -8.19) * mm, "end": v(-98.01, -8.16) * mm});
            skLineSegment(sketch, "E1109", {"start": v(-98.01, -8.16) * mm, "end": v(-98.64, -8.13) * mm});
            skLineSegment(sketch, "E1110", {"start": v(-98.64, -8.13) * mm, "end": v(-99.28, -8.1) * mm});
            skLineSegment(sketch, "E1111", {"start": v(-99.28, -8.1) * mm, "end": v(-99.91, -8.06) * mm});
            skLineSegment(sketch, "E1112", {"start": v(-99.91, -8.06) * mm, "end": v(-100.55, -8.03) * mm});
            skLineSegment(sketch, "E1113", {"start": v(-100.55, -8.03) * mm, "end": v(-101.18, -8) * mm});
            skLineSegment(sketch, "E1114", {"start": v(-101.18, -8) * mm, "end": v(-101.82, -7.96) * mm});
            skLineSegment(sketch, "E1115", {"start": v(-101.82, -7.96) * mm, "end": v(-102.45, -7.92) * mm});
            skLineSegment(sketch, "E1116", {"start": v(-102.45, -7.92) * mm, "end": v(-103.09, -7.88) * mm});
            skLineSegment(sketch, "E1117", {"start": v(-103.09, -7.88) * mm, "end": v(-103.72, -7.84) * mm});
            skLineSegment(sketch, "E1118", {"start": v(-103.72, -7.84) * mm, "end": v(-104.36, -7.8) * mm});
            skLineSegment(sketch, "E1119", {"start": v(-104.36, -7.8) * mm, "end": v(-104.99, -7.75) * mm});
            skLineSegment(sketch, "E1120", {"start": v(-104.99, -7.75) * mm, "end": v(-105.62, -7.7) * mm});
            skLineSegment(sketch, "E1121", {"start": v(-105.62, -7.7) * mm, "end": v(-106.26, -7.65) * mm});
            skLineSegment(sketch, "E1122", {"start": v(-106.26, -7.65) * mm, "end": v(-106.9, -7.6) * mm});
            skLineSegment(sketch, "E1123", {"start": v(-106.9, -7.6) * mm, "end": v(-107.53, -7.54) * mm});
            skLineSegment(sketch, "E1124", {"start": v(-107.53, -7.54) * mm, "end": v(-108.16, -7.49) * mm});
            skLineSegment(sketch, "E1125", {"start": v(-108.16, -7.49) * mm, "end": v(-108.8, -7.43) * mm});
            skLineSegment(sketch, "E1126", {"start": v(-108.8, -7.43) * mm, "end": v(-109.43, -7.37) * mm});
            skLineSegment(sketch, "E1127", {"start": v(-109.43, -7.37) * mm, "end": v(-110.06, -7.3) * mm});
            skLineSegment(sketch, "E1128", {"start": v(-110.06, -7.3) * mm, "end": v(-110.7, -7.24) * mm});
            skLineSegment(sketch, "E1129", {"start": v(-110.7, -7.24) * mm, "end": v(-111.33, -7.17) * mm});
            skLineSegment(sketch, "E1130", {"start": v(-111.33, -7.17) * mm, "end": v(-111.97, -7.1) * mm});
            skLineSegment(sketch, "E1131", {"start": v(-111.97, -7.1) * mm, "end": v(-112.6, -7.02) * mm});
            skLineSegment(sketch, "E1132", {"start": v(-112.6, -7.02) * mm, "end": v(-113.23, -6.94) * mm});
            skLineSegment(sketch, "E1133", {"start": v(-113.23, -6.94) * mm, "end": v(-113.87, -6.86) * mm});
            skLineSegment(sketch, "E1134", {"start": v(-113.87, -6.86) * mm, "end": v(-114.5, -6.78) * mm});
            skLineSegment(sketch, "E1135", {"start": v(-114.5, -6.78) * mm, "end": v(-115.13, -6.68) * mm});
            skLineSegment(sketch, "E1136", {"start": v(-115.13, -6.68) * mm, "end": v(-115.77, -6.58) * mm});
            skLineSegment(sketch, "E1137", {"start": v(-115.77, -6.58) * mm, "end": v(-116.4, -6.48) * mm});
            skLineSegment(sketch, "E1138", {"start": v(-116.4, -6.48) * mm, "end": v(-117.03, -6.38) * mm});
            skCircle(sketch, "E1139", {"center": v(-38.1, 0.27) * mm, "radius": 6 * mm});
            skLineSegment(sketch, "E1140", {"start": v(-44.1, 0.27) * mm, "end": v(-32.1, 0.27) * mm});
            skLineSegment(sketch, "E1141", {"start": v(-38.1, -2.73) * mm, "end": v(-38.1, 3.27) * mm});
            skCircle(sketch, "E1142", {"center": v(25.4, 0.1) * mm, "radius": 2 * mm});
            skLineSegment(sketch, "E1143", {"start": v(23.4, 0.1) * mm, "end": v(27.4, 0.1) * mm});
            skLineSegment(sketch, "E1144", {"start": v(25.4, -0.9) * mm, "end": v(25.4, 1.1) * mm});
            skLineSegment(sketch, "E1145", {"start": v(-117, 0.96) * mm, "end": v(-117.03, -6.38) * mm});
            skLineSegment(sketch, "E1146", {"start": v(61.39, 2.74) * mm, "end": v(61.37, -4.36) * mm});
            skSolve(sketch);
        }
        {
            var Q0;
            Q0=qSketchRegion(id+"F0",true);
            extrude(context, id + "F1", {"entities" : qUnion([Q0]), "depth" : 4 * mm, "offsetDistance" : 25 * mm});
        }
        {
            var Q0;
            Q0=qCreatedBy(makeId("Right.planeOp"),FACE);
            var sketch = newSketch(context, id + "F2", { "sketchPlane" : qUnion([Q0])});
            skLineSegment(sketch, "E1147", {"start": v(23.07, 0) * mm, "end": v(-78.09, 0) * mm, "construction": true});
            skCircle(sketch, "E1148", {"center": v(-94.75, 0) * mm, "radius": 4.1 * mm});
            skCircle(sketch, "E1149", {"center": v(-17.07, 0) * mm, "radius": 3.1 * mm});
            skSolve(sketch);
        }
        {
            var Q0;
            Q0 = qSketchRegion(id + "F2", true);
            extrude(context, id + "F3", {"entities" : qUnion([Q0]), "operationType" : NewBodyOperationType.REMOVE, "endBound" : BoundingType.THROUGH_ALL, "depth" : 25 * mm, "offsetDistance" : 25 * mm});
        }
        {
            var Q0;
            Q0=qCreatedBy(makeId("Right.planeOp"),FACE);
            var sketch = newSketch(context, id + "F4", { "sketchPlane" : qUnion([Q0])});
            skCircle(sketch, "E1150.0", {"center": v(-38.1, 0.27) * mm, "radius": 6 * mm});
            skSolve(sketch);
        }
        {
            var Q0;
            Q0 = qSketchRegion(id + "F4", true);
            var Q1;
            Q1=makeQuery(id+"F1.opExtrude","CAP_FACE",FACE,{"disambiguationData":[OSD([sQuery(id+"F0.wireOp",EDGE,"E577"),sQuery(id+"F0.wireOp",EDGE,"E578"),sQuery(id+"F0.wireOp",EDGE,"E579"),sQuery(id+"F0.wireOp",EDGE,"E580"),sQuery(id+"F0.wireOp",EDGE,"E581"),sQuery(id+"F0.wireOp",EDGE,"E582"),sQuery(id+"F0.wireOp",EDGE,"E583"),sQuery(id+"F0.wireOp",EDGE,"E584"),sQuery(id+"F0.wireOp",EDGE,"E585"),sQuery(id+"F0.wireOp",EDGE,"E586"),sQuery(id+"F0.wireOp",EDGE,"E587"),sQuery(id+"F0.wireOp",EDGE,"E588"),sQuery(id+"F0.wireOp",EDGE,"E589"),sQuery(id+"F0.wireOp",EDGE,"E590"),sQuery(id+"F0.wireOp",EDGE,"E591"),sQuery(id+"F0.wireOp",EDGE,"E592"),sQuery(id+"F0.wireOp",EDGE,"E593"),sQuery(id+"F0.wireOp",EDGE,"E594"),sQuery(id+"F0.wireOp",EDGE,"E595"),sQuery(id+"F0.wireOp",EDGE,"E596"),sQuery(id+"F0.wireOp",EDGE,"E597"),sQuery(id+"F0.wireOp",EDGE,"E598"),sQuery(id+"F0.wireOp",EDGE,"E599"),sQuery(id+"F0.wireOp",EDGE,"E600"),sQuery(id+"F0.wireOp",EDGE,"E601"),sQuery(id+"F0.wireOp",EDGE,"E602"),sQuery(id+"F0.wireOp",EDGE,"E603"),sQuery(id+"F0.wireOp",EDGE,"E604"),sQuery(id+"F0.wireOp",EDGE,"E605"),sQuery(id+"F0.wireOp",EDGE,"E606"),sQuery(id+"F0.wireOp",EDGE,"E607"),sQuery(id+"F0.wireOp",EDGE,"E608"),sQuery(id+"F0.wireOp",EDGE,"E609"),sQuery(id+"F0.wireOp",EDGE,"E610"),sQuery(id+"F0.wireOp",EDGE,"E611"),sQuery(id+"F0.wireOp",EDGE,"E612"),sQuery(id+"F0.wireOp",EDGE,"E613"),sQuery(id+"F0.wireOp",EDGE,"E614"),sQuery(id+"F0.wireOp",EDGE,"E615"),sQuery(id+"F0.wireOp",EDGE,"E616"),sQuery(id+"F0.wireOp",EDGE,"E617"),sQuery(id+"F0.wireOp",EDGE,"E618"),sQuery(id+"F0.wireOp",EDGE,"E619"),sQuery(id+"F0.wireOp",EDGE,"E620"),sQuery(id+"F0.wireOp",EDGE,"E621"),sQuery(id+"F0.wireOp",EDGE,"E622"),sQuery(id+"F0.wireOp",EDGE,"E623"),sQuery(id+"F0.wireOp",EDGE,"E624"),sQuery(id+"F0.wireOp",EDGE,"E625"),sQuery(id+"F0.wireOp",EDGE,"E626"),sQuery(id+"F0.wireOp",EDGE,"E627"),sQuery(id+"F0.wireOp",EDGE,"E628"),sQuery(id+"F0.wireOp",EDGE,"E629"),sQuery(id+"F0.wireOp",EDGE,"E630"),sQuery(id+"F0.wireOp",EDGE,"E631"),sQuery(id+"F0.wireOp",EDGE,"E632"),sQuery(id+"F0.wireOp",EDGE,"E633"),sQuery(id+"F0.wireOp",EDGE,"E634"),sQuery(id+"F0.wireOp",EDGE,"E635"),sQuery(id+"F0.wireOp",EDGE,"E636"),sQuery(id+"F0.wireOp",EDGE,"E637"),sQuery(id+"F0.wireOp",EDGE,"E638"),sQuery(id+"F0.wireOp",EDGE,"E639"),sQuery(id+"F0.wireOp",EDGE,"E640"),sQuery(id+"F0.wireOp",EDGE,"E641"),sQuery(id+"F0.wireOp",EDGE,"E642"),sQuery(id+"F0.wireOp",EDGE,"E643"),sQuery(id+"F0.wireOp",EDGE,"E644"),sQuery(id+"F0.wireOp",EDGE,"E645"),sQuery(id+"F0.wireOp",EDGE,"E646"),sQuery(id+"F0.wireOp",EDGE,"E647"),sQuery(id+"F0.wireOp",EDGE,"E648"),sQuery(id+"F0.wireOp",EDGE,"E649"),sQuery(id+"F0.wireOp",EDGE,"E650"),sQuery(id+"F0.wireOp",EDGE,"E651"),sQuery(id+"F0.wireOp",EDGE,"E652"),sQuery(id+"F0.wireOp",EDGE,"E653"),sQuery(id+"F0.wireOp",EDGE,"E654"),sQuery(id+"F0.wireOp",EDGE,"E655"),sQuery(id+"F0.wireOp",EDGE,"E656"),sQuery(id+"F0.wireOp",EDGE,"E657"),sQuery(id+"F0.wireOp",EDGE,"E658"),sQuery(id+"F0.wireOp",EDGE,"E659"),sQuery(id+"F0.wireOp",EDGE,"E660"),sQuery(id+"F0.wireOp",EDGE,"E661"),sQuery(id+"F0.wireOp",EDGE,"E662"),sQuery(id+"F0.wireOp",EDGE,"E663"),sQuery(id+"F0.wireOp",EDGE,"E664"),sQuery(id+"F0.wireOp",EDGE,"E665"),sQuery(id+"F0.wireOp",EDGE,"E666"),sQuery(id+"F0.wireOp",EDGE,"E667"),sQuery(id+"F0.wireOp",EDGE,"E668"),sQuery(id+"F0.wireOp",EDGE,"E669"),sQuery(id+"F0.wireOp",EDGE,"E670"),sQuery(id+"F0.wireOp",EDGE,"E671"),sQuery(id+"F0.wireOp",EDGE,"E672"),sQuery(id+"F0.wireOp",EDGE,"E673"),sQuery(id+"F0.wireOp",EDGE,"E674"),sQuery(id+"F0.wireOp",EDGE,"E675"),sQuery(id+"F0.wireOp",EDGE,"E676"),sQuery(id+"F0.wireOp",EDGE,"E677"),sQuery(id+"F0.wireOp",EDGE,"E678"),sQuery(id+"F0.wireOp",EDGE,"E679"),sQuery(id+"F0.wireOp",EDGE,"E680"),sQuery(id+"F0.wireOp",EDGE,"E681"),sQuery(id+"F0.wireOp",EDGE,"E682"),sQuery(id+"F0.wireOp",EDGE,"E683"),sQuery(id+"F0.wireOp",EDGE,"E684"),sQuery(id+"F0.wireOp",EDGE,"E685"),sQuery(id+"F0.wireOp",EDGE,"E686"),sQuery(id+"F0.wireOp",EDGE,"E687"),sQuery(id+"F0.wireOp",EDGE,"E688"),sQuery(id+"F0.wireOp",EDGE,"E689"),sQuery(id+"F0.wireOp",EDGE,"E690"),sQuery(id+"F0.wireOp",EDGE,"E691"),sQuery(id+"F0.wireOp",EDGE,"E692"),sQuery(id+"F0.wireOp",EDGE,"E693"),sQuery(id+"F0.wireOp",EDGE,"E694"),sQuery(id+"F0.wireOp",EDGE,"E695"),sQuery(id+"F0.wireOp",EDGE,"E696"),sQuery(id+"F0.wireOp",EDGE,"E697"),sQuery(id+"F0.wireOp",EDGE,"E698"),sQuery(id+"F0.wireOp",EDGE,"E699"),sQuery(id+"F0.wireOp",EDGE,"E700"),sQuery(id+"F0.wireOp",EDGE,"E701"),sQuery(id+"F0.wireOp",EDGE,"E702"),sQuery(id+"F0.wireOp",EDGE,"E703"),sQuery(id+"F0.wireOp",EDGE,"E704"),sQuery(id+"F0.wireOp",EDGE,"E705"),sQuery(id+"F0.wireOp",EDGE,"E706"),sQuery(id+"F0.wireOp",EDGE,"E707"),sQuery(id+"F0.wireOp",EDGE,"E708"),sQuery(id+"F0.wireOp",EDGE,"E709"),sQuery(id+"F0.wireOp",EDGE,"E710"),sQuery(id+"F0.wireOp",EDGE,"E711"),sQuery(id+"F0.wireOp",EDGE,"E712"),sQuery(id+"F0.wireOp",EDGE,"E713"),sQuery(id+"F0.wireOp",EDGE,"E714"),sQuery(id+"F0.wireOp",EDGE,"E715"),sQuery(id+"F0.wireOp",EDGE,"E716"),sQuery(id+"F0.wireOp",EDGE,"E717"),sQuery(id+"F0.wireOp",EDGE,"E718"),sQuery(id+"F0.wireOp",EDGE,"E719"),sQuery(id+"F0.wireOp",EDGE,"E720"),sQuery(id+"F0.wireOp",EDGE,"E721"),sQuery(id+"F0.wireOp",EDGE,"E722"),sQuery(id+"F0.wireOp",EDGE,"E723"),sQuery(id+"F0.wireOp",EDGE,"E724"),sQuery(id+"F0.wireOp",EDGE,"E725"),sQuery(id+"F0.wireOp",EDGE,"E726"),sQuery(id+"F0.wireOp",EDGE,"E727"),sQuery(id+"F0.wireOp",EDGE,"E728"),sQuery(id+"F0.wireOp",EDGE,"E729"),sQuery(id+"F0.wireOp",EDGE,"E730"),sQuery(id+"F0.wireOp",EDGE,"E731"),sQuery(id+"F0.wireOp",EDGE,"E732"),sQuery(id+"F0.wireOp",EDGE,"E733"),sQuery(id+"F0.wireOp",EDGE,"E734"),sQuery(id+"F0.wireOp",EDGE,"E735"),sQuery(id+"F0.wireOp",EDGE,"E736"),sQuery(id+"F0.wireOp",EDGE,"E737"),sQuery(id+"F0.wireOp",EDGE,"E738"),sQuery(id+"F0.wireOp",EDGE,"E739"),sQuery(id+"F0.wireOp",EDGE,"E740"),sQuery(id+"F0.wireOp",EDGE,"E741"),sQuery(id+"F0.wireOp",EDGE,"E742"),sQuery(id+"F0.wireOp",EDGE,"E743"),sQuery(id+"F0.wireOp",EDGE,"E744"),sQuery(id+"F0.wireOp",EDGE,"E745"),sQuery(id+"F0.wireOp",EDGE,"E746"),sQuery(id+"F0.wireOp",EDGE,"E747"),sQuery(id+"F0.wireOp",EDGE,"E748"),sQuery(id+"F0.wireOp",EDGE,"E749"),sQuery(id+"F0.wireOp",EDGE,"E750"),sQuery(id+"F0.wireOp",EDGE,"E751"),sQuery(id+"F0.wireOp",EDGE,"E752"),sQuery(id+"F0.wireOp",EDGE,"E753"),sQuery(id+"F0.wireOp",EDGE,"E754"),sQuery(id+"F0.wireOp",EDGE,"E755"),sQuery(id+"F0.wireOp",EDGE,"E756"),sQuery(id+"F0.wireOp",EDGE,"E757"),sQuery(id+"F0.wireOp",EDGE,"E758"),sQuery(id+"F0.wireOp",EDGE,"E759"),sQuery(id+"F0.wireOp",EDGE,"E760"),sQuery(id+"F0.wireOp",EDGE,"E761"),sQuery(id+"F0.wireOp",EDGE,"E762"),sQuery(id+"F0.wireOp",EDGE,"E763"),sQuery(id+"F0.wireOp",EDGE,"E764"),sQuery(id+"F0.wireOp",EDGE,"E765"),sQuery(id+"F0.wireOp",EDGE,"E766"),sQuery(id+"F0.wireOp",EDGE,"E767"),sQuery(id+"F0.wireOp",EDGE,"E768"),sQuery(id+"F0.wireOp",EDGE,"E769"),sQuery(id+"F0.wireOp",EDGE,"E770"),sQuery(id+"F0.wireOp",EDGE,"E771"),sQuery(id+"F0.wireOp",EDGE,"E772"),sQuery(id+"F0.wireOp",EDGE,"E773"),sQuery(id+"F0.wireOp",EDGE,"E774"),sQuery(id+"F0.wireOp",EDGE,"E775"),sQuery(id+"F0.wireOp",EDGE,"E776"),sQuery(id+"F0.wireOp",EDGE,"E777"),sQuery(id+"F0.wireOp",EDGE,"E778"),sQuery(id+"F0.wireOp",EDGE,"E779"),sQuery(id+"F0.wireOp",EDGE,"E780"),sQuery(id+"F0.wireOp",EDGE,"E781"),sQuery(id+"F0.wireOp",EDGE,"E782"),sQuery(id+"F0.wireOp",EDGE,"E783"),sQuery(id+"F0.wireOp",EDGE,"E784"),sQuery(id+"F0.wireOp",EDGE,"E785"),sQuery(id+"F0.wireOp",EDGE,"E786"),sQuery(id+"F0.wireOp",EDGE,"E787"),sQuery(id+"F0.wireOp",EDGE,"E788"),sQuery(id+"F0.wireOp",EDGE,"E789"),sQuery(id+"F0.wireOp",EDGE,"E790"),sQuery(id+"F0.wireOp",EDGE,"E791"),sQuery(id+"F0.wireOp",EDGE,"E792"),sQuery(id+"F0.wireOp",EDGE,"E793"),sQuery(id+"F0.wireOp",EDGE,"E794"),sQuery(id+"F0.wireOp",EDGE,"E795"),sQuery(id+"F0.wireOp",EDGE,"E796"),sQuery(id+"F0.wireOp",EDGE,"E797"),sQuery(id+"F0.wireOp",EDGE,"E798"),sQuery(id+"F0.wireOp",EDGE,"E799"),sQuery(id+"F0.wireOp",EDGE,"E800"),sQuery(id+"F0.wireOp",EDGE,"E801"),sQuery(id+"F0.wireOp",EDGE,"E802"),sQuery(id+"F0.wireOp",EDGE,"E803"),sQuery(id+"F0.wireOp",EDGE,"E804"),sQuery(id+"F0.wireOp",EDGE,"E805"),sQuery(id+"F0.wireOp",EDGE,"E806"),sQuery(id+"F0.wireOp",EDGE,"E807"),sQuery(id+"F0.wireOp",EDGE,"E808"),sQuery(id+"F0.wireOp",EDGE,"E809"),sQuery(id+"F0.wireOp",EDGE,"E810"),sQuery(id+"F0.wireOp",EDGE,"E811"),sQuery(id+"F0.wireOp",EDGE,"E812"),sQuery(id+"F0.wireOp",EDGE,"E813"),sQuery(id+"F0.wireOp",EDGE,"E814"),sQuery(id+"F0.wireOp",EDGE,"E815"),sQuery(id+"F0.wireOp",EDGE,"E816"),sQuery(id+"F0.wireOp",EDGE,"E817"),sQuery(id+"F0.wireOp",EDGE,"E818"),sQuery(id+"F0.wireOp",EDGE,"E819"),sQuery(id+"F0.wireOp",EDGE,"E820"),sQuery(id+"F0.wireOp",EDGE,"E821"),sQuery(id+"F0.wireOp",EDGE,"E822"),sQuery(id+"F0.wireOp",EDGE,"E823"),sQuery(id+"F0.wireOp",EDGE,"E824"),sQuery(id+"F0.wireOp",EDGE,"E825"),sQuery(id+"F0.wireOp",EDGE,"E826"),sQuery(id+"F0.wireOp",EDGE,"E827"),sQuery(id+"F0.wireOp",EDGE,"E828"),sQuery(id+"F0.wireOp",EDGE,"E829"),sQuery(id+"F0.wireOp",EDGE,"E830"),sQuery(id+"F0.wireOp",EDGE,"E831"),sQuery(id+"F0.wireOp",EDGE,"E832"),sQuery(id+"F0.wireOp",EDGE,"E833"),sQuery(id+"F0.wireOp",EDGE,"E834"),sQuery(id+"F0.wireOp",EDGE,"E835"),sQuery(id+"F0.wireOp",EDGE,"E836"),sQuery(id+"F0.wireOp",EDGE,"E837"),sQuery(id+"F0.wireOp",EDGE,"E838"),sQuery(id+"F0.wireOp",EDGE,"E839"),sQuery(id+"F0.wireOp",EDGE,"E840"),sQuery(id+"F0.wireOp",EDGE,"E841"),sQuery(id+"F0.wireOp",EDGE,"E842"),sQuery(id+"F0.wireOp",EDGE,"E843"),sQuery(id+"F0.wireOp",EDGE,"E844"),sQuery(id+"F0.wireOp",EDGE,"E845"),sQuery(id+"F0.wireOp",EDGE,"E846"),sQuery(id+"F0.wireOp",EDGE,"E847"),sQuery(id+"F0.wireOp",EDGE,"E848"),sQuery(id+"F0.wireOp",EDGE,"E849"),sQuery(id+"F0.wireOp",EDGE,"E850"),sQuery(id+"F0.wireOp",EDGE,"E851"),sQuery(id+"F0.wireOp",EDGE,"E852"),sQuery(id+"F0.wireOp",EDGE,"E853"),sQuery(id+"F0.wireOp",EDGE,"E854"),sQuery(id+"F0.wireOp",EDGE,"E855"),sQuery(id+"F0.wireOp",EDGE,"E856"),sQuery(id+"F0.wireOp",EDGE,"E857"),sQuery(id+"F0.wireOp",EDGE,"E858"),sQuery(id+"F0.wireOp",EDGE,"E859"),sQuery(id+"F0.wireOp",EDGE,"E860"),sQuery(id+"F0.wireOp",EDGE,"E861"),sQuery(id+"F0.wireOp",EDGE,"E862"),sQuery(id+"F0.wireOp",EDGE,"E863"),sQuery(id+"F0.wireOp",EDGE,"E864"),sQuery(id+"F0.wireOp",EDGE,"E865"),sQuery(id+"F0.wireOp",EDGE,"E866"),sQuery(id+"F0.wireOp",EDGE,"E867"),sQuery(id+"F0.wireOp",EDGE,"E868"),sQuery(id+"F0.wireOp",EDGE,"E869"),sQuery(id+"F0.wireOp",EDGE,"E870"),sQuery(id+"F0.wireOp",EDGE,"E871"),sQuery(id+"F0.wireOp",EDGE,"E872"),sQuery(id+"F0.wireOp",EDGE,"E873"),sQuery(id+"F0.wireOp",EDGE,"E874"),sQuery(id+"F0.wireOp",EDGE,"E875"),sQuery(id+"F0.wireOp",EDGE,"E876"),sQuery(id+"F0.wireOp",EDGE,"E877"),sQuery(id+"F0.wireOp",EDGE,"E878"),sQuery(id+"F0.wireOp",EDGE,"E879"),sQuery(id+"F0.wireOp",EDGE,"E880"),sQuery(id+"F0.wireOp",EDGE,"E881"),sQuery(id+"F0.wireOp",EDGE,"E882"),sQuery(id+"F0.wireOp",EDGE,"E883"),sQuery(id+"F0.wireOp",EDGE,"E884"),sQuery(id+"F0.wireOp",EDGE,"E885"),sQuery(id+"F0.wireOp",EDGE,"E886"),sQuery(id+"F0.wireOp",EDGE,"E887"),sQuery(id+"F0.wireOp",EDGE,"E888"),sQuery(id+"F0.wireOp",EDGE,"E889"),sQuery(id+"F0.wireOp",EDGE,"E890"),sQuery(id+"F0.wireOp",EDGE,"E891"),sQuery(id+"F0.wireOp",EDGE,"E892"),sQuery(id+"F0.wireOp",EDGE,"E893"),sQuery(id+"F0.wireOp",EDGE,"E894"),sQuery(id+"F0.wireOp",EDGE,"E895"),sQuery(id+"F0.wireOp",EDGE,"E896"),sQuery(id+"F0.wireOp",EDGE,"E897"),sQuery(id+"F0.wireOp",EDGE,"E898"),sQuery(id+"F0.wireOp",EDGE,"E899"),sQuery(id+"F0.wireOp",EDGE,"E900"),sQuery(id+"F0.wireOp",EDGE,"E901"),sQuery(id+"F0.wireOp",EDGE,"E902"),sQuery(id+"F0.wireOp",EDGE,"E903"),sQuery(id+"F0.wireOp",EDGE,"E904"),sQuery(id+"F0.wireOp",EDGE,"E905"),sQuery(id+"F0.wireOp",EDGE,"E906"),sQuery(id+"F0.wireOp",EDGE,"E907"),sQuery(id+"F0.wireOp",EDGE,"E908"),sQuery(id+"F0.wireOp",EDGE,"E909"),sQuery(id+"F0.wireOp",EDGE,"E910"),sQuery(id+"F0.wireOp",EDGE,"E911"),sQuery(id+"F0.wireOp",EDGE,"E912"),sQuery(id+"F0.wireOp",EDGE,"E913"),sQuery(id+"F0.wireOp",EDGE,"E914"),sQuery(id+"F0.wireOp",EDGE,"E915"),sQuery(id+"F0.wireOp",EDGE,"E916"),sQuery(id+"F0.wireOp",EDGE,"E917"),sQuery(id+"F0.wireOp",EDGE,"E918"),sQuery(id+"F0.wireOp",EDGE,"E919"),sQuery(id+"F0.wireOp",EDGE,"E920"),sQuery(id+"F0.wireOp",EDGE,"E921"),sQuery(id+"F0.wireOp",EDGE,"E922"),sQuery(id+"F0.wireOp",EDGE,"E923"),sQuery(id+"F0.wireOp",EDGE,"E924"),sQuery(id+"F0.wireOp",EDGE,"E925"),sQuery(id+"F0.wireOp",EDGE,"E926"),sQuery(id+"F0.wireOp",EDGE,"E927"),sQuery(id+"F0.wireOp",EDGE,"E928"),sQuery(id+"F0.wireOp",EDGE,"E929"),sQuery(id+"F0.wireOp",EDGE,"E930"),sQuery(id+"F0.wireOp",EDGE,"E931"),sQuery(id+"F0.wireOp",EDGE,"E932"),sQuery(id+"F0.wireOp",EDGE,"E933"),sQuery(id+"F0.wireOp",EDGE,"E934"),sQuery(id+"F0.wireOp",EDGE,"E935"),sQuery(id+"F0.wireOp",EDGE,"E936"),sQuery(id+"F0.wireOp",EDGE,"E937"),sQuery(id+"F0.wireOp",EDGE,"E938"),sQuery(id+"F0.wireOp",EDGE,"E939"),sQuery(id+"F0.wireOp",EDGE,"E940"),sQuery(id+"F0.wireOp",EDGE,"E941"),sQuery(id+"F0.wireOp",EDGE,"E942"),sQuery(id+"F0.wireOp",EDGE,"E943"),sQuery(id+"F0.wireOp",EDGE,"E944"),sQuery(id+"F0.wireOp",EDGE,"E945"),sQuery(id+"F0.wireOp",EDGE,"E946"),sQuery(id+"F0.wireOp",EDGE,"E947"),sQuery(id+"F0.wireOp",EDGE,"E948"),sQuery(id+"F0.wireOp",EDGE,"E949"),sQuery(id+"F0.wireOp",EDGE,"E950"),sQuery(id+"F0.wireOp",EDGE,"E951"),sQuery(id+"F0.wireOp",EDGE,"E952"),sQuery(id+"F0.wireOp",EDGE,"E953"),sQuery(id+"F0.wireOp",EDGE,"E954"),sQuery(id+"F0.wireOp",EDGE,"E955"),sQuery(id+"F0.wireOp",EDGE,"E956"),sQuery(id+"F0.wireOp",EDGE,"E957"),sQuery(id+"F0.wireOp",EDGE,"E958"),sQuery(id+"F0.wireOp",EDGE,"E959"),sQuery(id+"F0.wireOp",EDGE,"E960"),sQuery(id+"F0.wireOp",EDGE,"E961"),sQuery(id+"F0.wireOp",EDGE,"E962"),sQuery(id+"F0.wireOp",EDGE,"E963"),sQuery(id+"F0.wireOp",EDGE,"E964"),sQuery(id+"F0.wireOp",EDGE,"E965"),sQuery(id+"F0.wireOp",EDGE,"E966"),sQuery(id+"F0.wireOp",EDGE,"E967"),sQuery(id+"F0.wireOp",EDGE,"E968"),sQuery(id+"F0.wireOp",EDGE,"E969"),sQuery(id+"F0.wireOp",EDGE,"E970"),sQuery(id+"F0.wireOp",EDGE,"E971"),sQuery(id+"F0.wireOp",EDGE,"E972"),sQuery(id+"F0.wireOp",EDGE,"E973"),sQuery(id+"F0.wireOp",EDGE,"E974"),sQuery(id+"F0.wireOp",EDGE,"E975"),sQuery(id+"F0.wireOp",EDGE,"E976"),sQuery(id+"F0.wireOp",EDGE,"E977"),sQuery(id+"F0.wireOp",EDGE,"E978"),sQuery(id+"F0.wireOp",EDGE,"E979"),sQuery(id+"F0.wireOp",EDGE,"E980"),sQuery(id+"F0.wireOp",EDGE,"E981"),sQuery(id+"F0.wireOp",EDGE,"E982"),sQuery(id+"F0.wireOp",EDGE,"E983"),sQuery(id+"F0.wireOp",EDGE,"E984"),sQuery(id+"F0.wireOp",EDGE,"E985"),sQuery(id+"F0.wireOp",EDGE,"E986"),sQuery(id+"F0.wireOp",EDGE,"E987"),sQuery(id+"F0.wireOp",EDGE,"E988"),sQuery(id+"F0.wireOp",EDGE,"E989"),sQuery(id+"F0.wireOp",EDGE,"E990"),sQuery(id+"F0.wireOp",EDGE,"E991"),sQuery(id+"F0.wireOp",EDGE,"E992"),sQuery(id+"F0.wireOp",EDGE,"E993"),sQuery(id+"F0.wireOp",EDGE,"E994"),sQuery(id+"F0.wireOp",EDGE,"E995"),sQuery(id+"F0.wireOp",EDGE,"E996"),sQuery(id+"F0.wireOp",EDGE,"E997"),sQuery(id+"F0.wireOp",EDGE,"E998"),sQuery(id+"F0.wireOp",EDGE,"E999"),sQuery(id+"F0.wireOp",EDGE,"E1000"),sQuery(id+"F0.wireOp",EDGE,"E1001"),sQuery(id+"F0.wireOp",EDGE,"E1002"),sQuery(id+"F0.wireOp",EDGE,"E1003"),sQuery(id+"F0.wireOp",EDGE,"E1004"),sQuery(id+"F0.wireOp",EDGE,"E1005"),sQuery(id+"F0.wireOp",EDGE,"E1006"),sQuery(id+"F0.wireOp",EDGE,"E1007"),sQuery(id+"F0.wireOp",EDGE,"E1008"),sQuery(id+"F0.wireOp",EDGE,"E1009"),sQuery(id+"F0.wireOp",EDGE,"E1010"),sQuery(id+"F0.wireOp",EDGE,"E1011"),sQuery(id+"F0.wireOp",EDGE,"E1012"),sQuery(id+"F0.wireOp",EDGE,"E1013"),sQuery(id+"F0.wireOp",EDGE,"E1014"),sQuery(id+"F0.wireOp",EDGE,"E1015"),sQuery(id+"F0.wireOp",EDGE,"E1016"),sQuery(id+"F0.wireOp",EDGE,"E1017"),sQuery(id+"F0.wireOp",EDGE,"E1018"),sQuery(id+"F0.wireOp",EDGE,"E1019"),sQuery(id+"F0.wireOp",EDGE,"E1020"),sQuery(id+"F0.wireOp",EDGE,"E1021"),sQuery(id+"F0.wireOp",EDGE,"E1022"),sQuery(id+"F0.wireOp",EDGE,"E1023"),sQuery(id+"F0.wireOp",EDGE,"E1024"),sQuery(id+"F0.wireOp",EDGE,"E1025"),sQuery(id+"F0.wireOp",EDGE,"E1026"),sQuery(id+"F0.wireOp",EDGE,"E1027"),sQuery(id+"F0.wireOp",EDGE,"E1028"),sQuery(id+"F0.wireOp",EDGE,"E1029"),sQuery(id+"F0.wireOp",EDGE,"E1030"),sQuery(id+"F0.wireOp",EDGE,"E1031"),sQuery(id+"F0.wireOp",EDGE,"E1032"),sQuery(id+"F0.wireOp",EDGE,"E1033"),sQuery(id+"F0.wireOp",EDGE,"E1034"),sQuery(id+"F0.wireOp",EDGE,"E1035"),sQuery(id+"F0.wireOp",EDGE,"E1036"),sQuery(id+"F0.wireOp",EDGE,"E1037"),sQuery(id+"F0.wireOp",EDGE,"E1038"),sQuery(id+"F0.wireOp",EDGE,"E1039"),sQuery(id+"F0.wireOp",EDGE,"E1040"),sQuery(id+"F0.wireOp",EDGE,"E1041"),sQuery(id+"F0.wireOp",EDGE,"E1042"),sQuery(id+"F0.wireOp",EDGE,"E1043"),sQuery(id+"F0.wireOp",EDGE,"E1044"),sQuery(id+"F0.wireOp",EDGE,"E1045"),sQuery(id+"F0.wireOp",EDGE,"E1046"),sQuery(id+"F0.wireOp",EDGE,"E1047"),sQuery(id+"F0.wireOp",EDGE,"E1048"),sQuery(id+"F0.wireOp",EDGE,"E1049"),sQuery(id+"F0.wireOp",EDGE,"E1050"),sQuery(id+"F0.wireOp",EDGE,"E1051"),sQuery(id+"F0.wireOp",EDGE,"E1052"),sQuery(id+"F0.wireOp",EDGE,"E1053"),sQuery(id+"F0.wireOp",EDGE,"E1054"),sQuery(id+"F0.wireOp",EDGE,"E1055"),sQuery(id+"F0.wireOp",EDGE,"E1056"),sQuery(id+"F0.wireOp",EDGE,"E1057"),sQuery(id+"F0.wireOp",EDGE,"E1058"),sQuery(id+"F0.wireOp",EDGE,"E1059"),sQuery(id+"F0.wireOp",EDGE,"E1060"),sQuery(id+"F0.wireOp",EDGE,"E1061"),sQuery(id+"F0.wireOp",EDGE,"E1062"),sQuery(id+"F0.wireOp",EDGE,"E1063"),sQuery(id+"F0.wireOp",EDGE,"E1064"),sQuery(id+"F0.wireOp",EDGE,"E1065"),sQuery(id+"F0.wireOp",EDGE,"E1066"),sQuery(id+"F0.wireOp",EDGE,"E1067"),sQuery(id+"F0.wireOp",EDGE,"E1068"),sQuery(id+"F0.wireOp",EDGE,"E1069"),sQuery(id+"F0.wireOp",EDGE,"E1070"),sQuery(id+"F0.wireOp",EDGE,"E1071"),sQuery(id+"F0.wireOp",EDGE,"E1072"),sQuery(id+"F0.wireOp",EDGE,"E1073"),sQuery(id+"F0.wireOp",EDGE,"E1074"),sQuery(id+"F0.wireOp",EDGE,"E1075"),sQuery(id+"F0.wireOp",EDGE,"E1076"),sQuery(id+"F0.wireOp",EDGE,"E1077"),sQuery(id+"F0.wireOp",EDGE,"E1078"),sQuery(id+"F0.wireOp",EDGE,"E1079"),sQuery(id+"F0.wireOp",EDGE,"E1080"),sQuery(id+"F0.wireOp",EDGE,"E1081"),sQuery(id+"F0.wireOp",EDGE,"E1082"),sQuery(id+"F0.wireOp",EDGE,"E1083"),sQuery(id+"F0.wireOp",EDGE,"E1084"),sQuery(id+"F0.wireOp",EDGE,"E1085"),sQuery(id+"F0.wireOp",EDGE,"E1086"),sQuery(id+"F0.wireOp",EDGE,"E1087"),sQuery(id+"F0.wireOp",EDGE,"E1088"),sQuery(id+"F0.wireOp",EDGE,"E1089"),sQuery(id+"F0.wireOp",EDGE,"E1090"),sQuery(id+"F0.wireOp",EDGE,"E1091"),sQuery(id+"F0.wireOp",EDGE,"E1092"),sQuery(id+"F0.wireOp",EDGE,"E1093"),sQuery(id+"F0.wireOp",EDGE,"E1094"),sQuery(id+"F0.wireOp",EDGE,"E1095"),sQuery(id+"F0.wireOp",EDGE,"E1096"),sQuery(id+"F0.wireOp",EDGE,"E1097"),sQuery(id+"F0.wireOp",EDGE,"E1098"),sQuery(id+"F0.wireOp",EDGE,"E1099"),sQuery(id+"F0.wireOp",EDGE,"E1100"),sQuery(id+"F0.wireOp",EDGE,"E1101"),sQuery(id+"F0.wireOp",EDGE,"E1102"),sQuery(id+"F0.wireOp",EDGE,"E1103"),sQuery(id+"F0.wireOp",EDGE,"E1104"),sQuery(id+"F0.wireOp",EDGE,"E1105"),sQuery(id+"F0.wireOp",EDGE,"E1106"),sQuery(id+"F0.wireOp",EDGE,"E1107"),sQuery(id+"F0.wireOp",EDGE,"E1108"),sQuery(id+"F0.wireOp",EDGE,"E1109"),sQuery(id+"F0.wireOp",EDGE,"E1110"),sQuery(id+"F0.wireOp",EDGE,"E1111"),sQuery(id+"F0.wireOp",EDGE,"E1112"),sQuery(id+"F0.wireOp",EDGE,"E1113"),sQuery(id+"F0.wireOp",EDGE,"E1114"),sQuery(id+"F0.wireOp",EDGE,"E1115"),sQuery(id+"F0.wireOp",EDGE,"E1116"),sQuery(id+"F0.wireOp",EDGE,"E1117"),sQuery(id+"F0.wireOp",EDGE,"E1118"),sQuery(id+"F0.wireOp",EDGE,"E1119"),sQuery(id+"F0.wireOp",EDGE,"E1120"),sQuery(id+"F0.wireOp",EDGE,"E1121"),sQuery(id+"F0.wireOp",EDGE,"E1122"),sQuery(id+"F0.wireOp",EDGE,"E1123"),sQuery(id+"F0.wireOp",EDGE,"E1124"),sQuery(id+"F0.wireOp",EDGE,"E1125"),sQuery(id+"F0.wireOp",EDGE,"E1126"),sQuery(id+"F0.wireOp",EDGE,"E1127"),sQuery(id+"F0.wireOp",EDGE,"E1128"),sQuery(id+"F0.wireOp",EDGE,"E1129"),sQuery(id+"F0.wireOp",EDGE,"E1130"),sQuery(id+"F0.wireOp",EDGE,"E1131"),sQuery(id+"F0.wireOp",EDGE,"E1132"),sQuery(id+"F0.wireOp",EDGE,"E1133"),sQuery(id+"F0.wireOp",EDGE,"E1134"),sQuery(id+"F0.wireOp",EDGE,"E1135"),sQuery(id+"F0.wireOp",EDGE,"E1136"),sQuery(id+"F0.wireOp",EDGE,"E1137"),sQuery(id+"F0.wireOp",EDGE,"E1138"),sQuery(id+"F0.wireOp",EDGE,"E1139"),sQuery(id+"F0.wireOp",EDGE,"E1142"),sQuery(id+"F0.wireOp",EDGE,"E1145"),sQuery(id+"F0.wireOp",EDGE,"E1146")])],"isStart":false});
            extrude(context, id + "F5", {"entities" : qUnion([Q0]), "operationType" : NewBodyOperationType.ADD, "endBound" : BoundingType.UP_TO_SURFACE, "depth" : 25 * mm, "endBoundEntityFace" : qUnion([Q1]), "offsetDistance" : 25 * mm});
        }
    });
